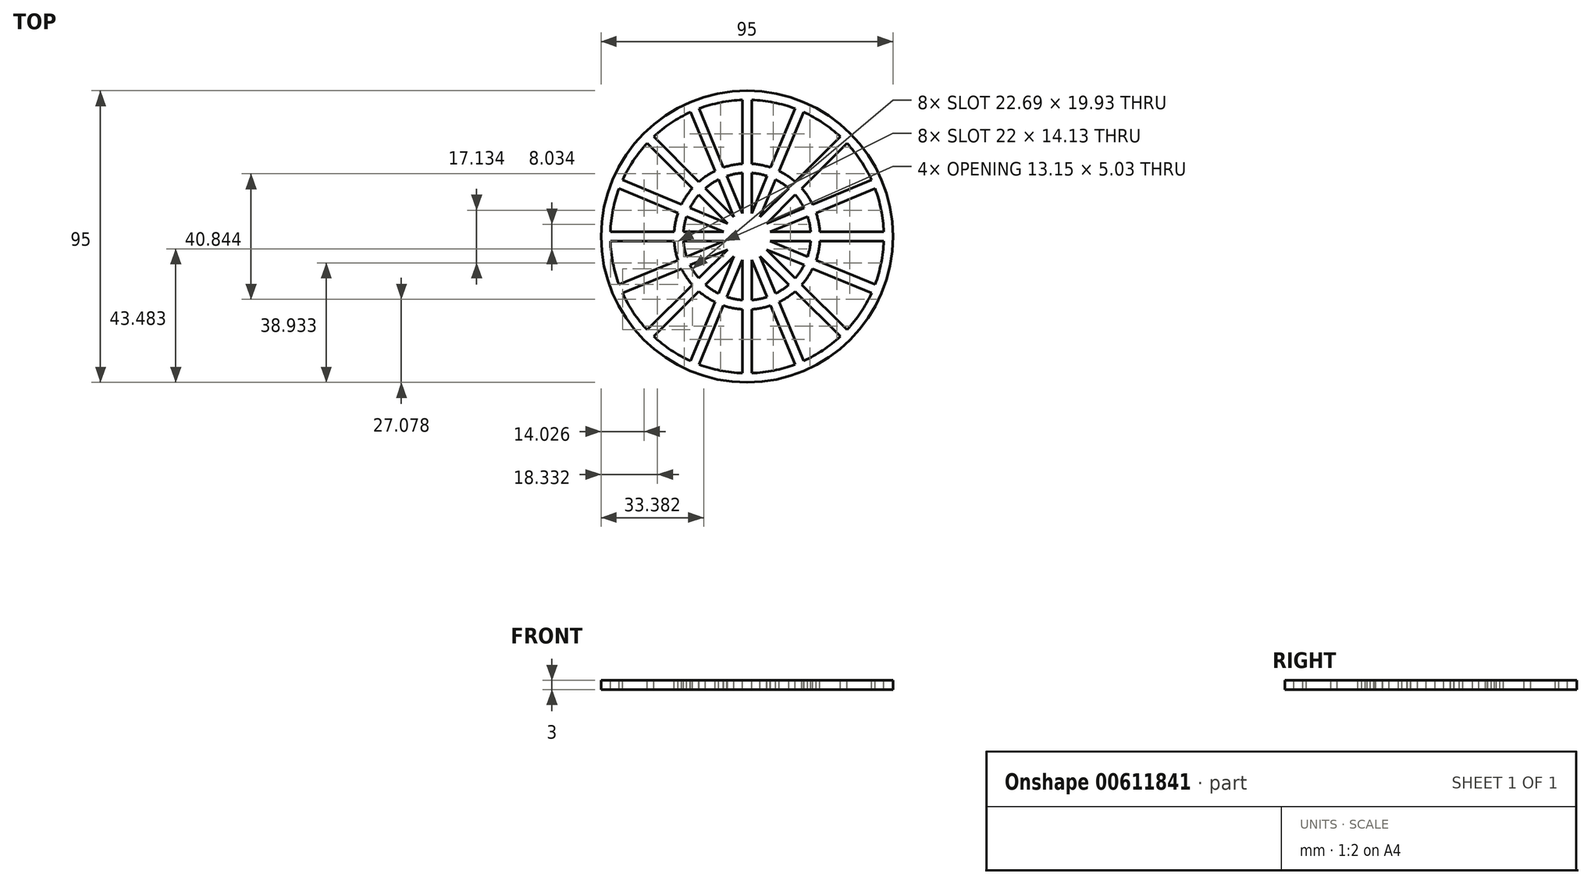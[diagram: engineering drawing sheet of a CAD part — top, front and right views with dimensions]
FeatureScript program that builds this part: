
annotation { "Feature Type Name" : "Feature", "Feature Type Description" : "" }
export const myFeature = defineFeature(function(context is Context, id is Id, definition is map)
    precondition{}
    {
        {
            assignVariable(context, id + "F0", {"name" : "b", "anyValue" : 3});
        }
        {
            var Q0;
            Q0=qCreatedBy(makeId("Top.planeOp"),FACE);
            var sketch = newSketch(context, id + "F1", { "sketchPlane" : qUnion([Q0])});
            skCircle(sketch, "E0", {"center": v(0, 0) * mm, "radius": 47.5 * mm});
            skCircle(sketch, "E1.0", {"center": v(0, 0) * mm, "radius": 44.5 * mm});
            skCircle(sketch, "E2", {"center": v(0, 0) * mm, "radius": 23.75 * mm});
            skCircle(sketch, "E3.0", {"center": v(0, 0) * mm, "radius": 20.75 * mm});
            skCircle(sketch, "E4", {"center": v(0, 0) * mm, "radius": 7.69 * mm});
            skLineSegment(sketch, "E5", {"start": v(0, 47.5) * mm, "end": v(0, -47.5) * mm, "construction": true});
            skLineSegment(sketch, "E6", {"start": v(1.5, 47.48) * mm, "end": v(1.5, 0) * mm});
            skLineSegment(sketch, "E7", {"start": v(1.5, 0) * mm, "end": v(-1.5, 0) * mm});
            skLineSegment(sketch, "E8", {"start": v(-1.5, 0) * mm, "end": v(-1.5, 47.48) * mm});
            skLineSegment(sketch, "E9.1.0", {"start": v(-1.39, -0.57) * mm, "end": v(-19.55, 43.29) * mm});
            skLineSegment(sketch, "E9.1.1", {"start": v(-16.78, 44.44) * mm, "end": v(1.39, 0.57) * mm});
            skLineSegment(sketch, "E9.2.0", {"start": v(-1.06, -1.06) * mm, "end": v(-34.63, 32.51) * mm});
            skLineSegment(sketch, "E9.2.1", {"start": v(-32.51, 34.63) * mm, "end": v(1.06, 1.06) * mm});
            skLineSegment(sketch, "E9.3.0", {"start": v(-0.57, -1.39) * mm, "end": v(-44.44, 16.78) * mm});
            skLineSegment(sketch, "E9.3.1", {"start": v(-43.29, 19.55) * mm, "end": v(0.57, 1.39) * mm});
            skLineSegment(sketch, "E9.4.0", {"start": v(0, -1.5) * mm, "end": v(-47.48, -1.5) * mm});
            skLineSegment(sketch, "E9.4.1", {"start": v(-47.48, 1.5) * mm, "end": v(0, 1.5) * mm});
            skLineSegment(sketch, "E9.5.0", {"start": v(0.57, -1.39) * mm, "end": v(-43.29, -19.55) * mm});
            skLineSegment(sketch, "E9.5.1", {"start": v(-44.44, -16.78) * mm, "end": v(-0.57, 1.39) * mm});
            skLineSegment(sketch, "E9.6.0", {"start": v(1.06, -1.06) * mm, "end": v(-32.51, -34.63) * mm});
            skLineSegment(sketch, "E9.6.1", {"start": v(-34.63, -32.51) * mm, "end": v(-1.06, 1.06) * mm});
            skLineSegment(sketch, "E9.7.0", {"start": v(1.39, -0.57) * mm, "end": v(-16.78, -44.44) * mm});
            skLineSegment(sketch, "E9.7.1", {"start": v(-19.55, -43.29) * mm, "end": v(-1.39, 0.57) * mm});
            skLineSegment(sketch, "E9.8.0", {"start": v(1.5, 0) * mm, "end": v(1.5, -47.48) * mm});
            skLineSegment(sketch, "E9.8.1", {"start": v(-1.5, -47.48) * mm, "end": v(-1.5, 0) * mm});
            skLineSegment(sketch, "E9.9.0", {"start": v(1.39, 0.57) * mm, "end": v(19.55, -43.29) * mm});
            skLineSegment(sketch, "E9.9.1", {"start": v(16.78, -44.44) * mm, "end": v(-1.39, -0.57) * mm});
            skLineSegment(sketch, "E9.10.0", {"start": v(1.06, 1.06) * mm, "end": v(34.63, -32.51) * mm});
            skLineSegment(sketch, "E9.10.1", {"start": v(32.51, -34.63) * mm, "end": v(-1.06, -1.06) * mm});
            skLineSegment(sketch, "E9.11.0", {"start": v(0.57, 1.39) * mm, "end": v(44.44, -16.78) * mm});
            skLineSegment(sketch, "E9.11.1", {"start": v(43.29, -19.55) * mm, "end": v(-0.57, -1.39) * mm});
            skLineSegment(sketch, "E9.12.0", {"start": v(0, 1.5) * mm, "end": v(47.48, 1.5) * mm});
            skLineSegment(sketch, "E9.12.1", {"start": v(47.48, -1.5) * mm, "end": v(0, -1.5) * mm});
            skLineSegment(sketch, "E9.13.0", {"start": v(-0.57, 1.39) * mm, "end": v(43.29, 19.55) * mm});
            skLineSegment(sketch, "E9.13.1", {"start": v(44.44, 16.78) * mm, "end": v(0.57, -1.39) * mm});
            skLineSegment(sketch, "E9.14.0", {"start": v(-1.06, 1.06) * mm, "end": v(32.51, 34.63) * mm});
            skLineSegment(sketch, "E9.14.1", {"start": v(34.63, 32.51) * mm, "end": v(1.06, -1.06) * mm});
            skLineSegment(sketch, "E9.15.0", {"start": v(-1.39, 0.57) * mm, "end": v(16.78, 44.44) * mm});
            skLineSegment(sketch, "E9.15.1", {"start": v(19.55, 43.29) * mm, "end": v(1.39, -0.57) * mm});
            skPoint(sketch, "E10", {"position": v(-1.5, 7.54) * mm});
            skSolve(sketch);
        }
        {
            var Q0;
            {var subQ0=sQuery(id+"F1.wireOp",EDGE,"E9.2.1");var subQ1=sQuery(id+"F1.wireOp",EDGE,"E1.0");var subQ2=makeQuery(id+"F1.imprint","INTERSECT",VERTEX,{"derivedFrom":[subQ1,subQ0]});Q0=makeQuery(id+"F1.imprint","IMPRINT",FACE,{"disambiguationData":[TD([[makeQuery(id+"F1.imprint","IMPRINT",EDGE,{"disambiguationData":[TD([[subQ2,-1.0]])],"derivedFrom":subQ1}),1.0]])]});}
            var Q1;
            {var subQ0=sQuery(id+"F1.wireOp",EDGE,"E9.2.1");var subQ1=sQuery(id+"F1.wireOp",EDGE,"E2");var subQ2=makeQuery(id+"F1.imprint","INTERSECT",VERTEX,{"derivedFrom":[subQ1,subQ0]});Q1=makeQuery(id+"F1.imprint","IMPRINT",FACE,{"disambiguationData":[TD([[makeQuery(id+"F1.imprint","IMPRINT",EDGE,{"disambiguationData":[TD([[subQ2,-1.0]])],"derivedFrom":subQ1}),1.0]])]});}
            var Q2;
            {var subQ0=sQuery(id+"F1.wireOp",EDGE,"E9.2.1");var subQ1=sQuery(id+"F1.wireOp",EDGE,"E3.0");var subQ2=makeQuery(id+"F1.imprint","INTERSECT",VERTEX,{"derivedFrom":[subQ1,subQ0]});Q2=makeQuery(id+"F1.imprint","IMPRINT",FACE,{"disambiguationData":[TD([[makeQuery(id+"F1.imprint","IMPRINT",EDGE,{"disambiguationData":[TD([[subQ2,-1.0]])],"derivedFrom":subQ1}),1.0]])]});}
            var Q3;
            {var subQ0=sQuery(id+"F1.wireOp",EDGE,"E8");var subQ3=sQuery(id+"F1.wireOp",EDGE,"E9.2.1");var subQ5=makeQuery(id+"F1.imprint","INTERSECT",VERTEX,{"derivedFrom":[subQ0,subQ3]});Q3=makeQuery(id+"F1.imprint","IMPRINT",FACE,{"disambiguationData":[TD([[makeQuery(id+"F1.imprint","IMPRINT",EDGE,{"disambiguationData":[TD([[subQ5,-1.0]])],"derivedFrom":subQ0}),1.0]])]});}
            var Q4;
            {var subQ0=sQuery(id+"F1.wireOp",EDGE,"E9.15.1");var subQ1=sQuery(id+"F1.wireOp",EDGE,"E9.12.0");var subQ2=makeQuery(id+"F1.imprint","INTERSECT",VERTEX,{"derivedFrom":[subQ1,subQ0]});Q4=makeQuery(id+"F1.imprint","IMPRINT",FACE,{"disambiguationData":[TD([[makeQuery(id+"F1.imprint","IMPRINT",EDGE,{"disambiguationData":[TD([[subQ2,-1.0]])],"derivedFrom":subQ1}),1.0]])]});}
            var Q5;
            {var subQ0=sQuery(id+"F1.wireOp",EDGE,"E9.9.1");var subQ1=sQuery(id+"F1.wireOp",EDGE,"E9.4.0");var subQ2=makeQuery(id+"F1.imprint","INTERSECT",VERTEX,{"derivedFrom":[subQ1,subQ0]});Q5=makeQuery(id+"F1.imprint","IMPRINT",FACE,{"disambiguationData":[TD([[makeQuery(id+"F1.imprint","IMPRINT",EDGE,{"disambiguationData":[TD([[subQ2,-1.0]])],"derivedFrom":subQ1}),1.0]])]});}
            var Q6;
            {var subQ0=sQuery(id+"F1.wireOp",EDGE,"E9.8.1");var subQ1=sQuery(id+"F1.wireOp",EDGE,"E9.2.0");var subQ2=makeQuery(id+"F1.imprint","INTERSECT",VERTEX,{"derivedFrom":[subQ1,subQ0]});Q6=makeQuery(id+"F1.imprint","IMPRINT",FACE,{"disambiguationData":[TD([[makeQuery(id+"F1.imprint","IMPRINT",EDGE,{"disambiguationData":[TD([[subQ2,-1.0]])],"derivedFrom":subQ1}),1.0]])]});}
            var Q7;
            {var subQ0=sQuery(id+"F1.wireOp",EDGE,"E9.5.0");var subQ3=sQuery(id+"F1.wireOp",EDGE,"E9.7.1");var subQ5=makeQuery(id+"F1.imprint","INTERSECT",VERTEX,{"derivedFrom":[subQ0,subQ3]});Q7=makeQuery(id+"F1.imprint","IMPRINT",FACE,{"disambiguationData":[TD([[makeQuery(id+"F1.imprint","IMPRINT",EDGE,{"disambiguationData":[TD([[subQ5,-1.0]])],"derivedFrom":subQ0}),1.0]])]});}
            var Q8;
            {var subQ0=sQuery(id+"F1.wireOp",EDGE,"E9.4.1");var subQ1=sQuery(id+"F1.wireOp",EDGE,"E9.1.0");var subQ2=makeQuery(id+"F1.imprint","INTERSECT",VERTEX,{"derivedFrom":[subQ1,subQ0]});Q8=makeQuery(id+"F1.imprint","IMPRINT",FACE,{"disambiguationData":[TD([[makeQuery(id+"F1.imprint","IMPRINT",EDGE,{"disambiguationData":[TD([[subQ2,-1.0]])],"derivedFrom":subQ1}),1.0]])]});}
            var Q9;
            {var subQ0=sQuery(id+"F1.wireOp",EDGE,"E9.7.1");var subQ1=sQuery(id+"F1.wireOp",EDGE,"E9.2.0");var subQ2=makeQuery(id+"F1.imprint","INTERSECT",VERTEX,{"derivedFrom":[subQ1,subQ0]});Q9=makeQuery(id+"F1.imprint","IMPRINT",FACE,{"disambiguationData":[TD([[makeQuery(id+"F1.imprint","IMPRINT",EDGE,{"disambiguationData":[TD([[subQ2,-1.0]])],"derivedFrom":subQ1}),1.0]])]});}
            var Q10;
            {var subQ0=sQuery(id+"F1.wireOp",EDGE,"E9.4.0");var subQ3=sQuery(id+"F1.wireOp",EDGE,"E9.6.1");var subQ5=makeQuery(id+"F1.imprint","INTERSECT",VERTEX,{"derivedFrom":[subQ0,subQ3]});Q10=makeQuery(id+"F1.imprint","IMPRINT",FACE,{"disambiguationData":[TD([[makeQuery(id+"F1.imprint","IMPRINT",EDGE,{"disambiguationData":[TD([[subQ5,-1.0]])],"derivedFrom":subQ0}),1.0]])]});}
            var Q11;
            {var subQ0=sQuery(id+"F1.wireOp",EDGE,"E9.13.0");var subQ1=sQuery(id+"F1.wireOp",EDGE,"E6");var subQ2=makeQuery(id+"F1.imprint","INTERSECT",VERTEX,{"derivedFrom":[subQ1,subQ0]});Q11=makeQuery(id+"F1.imprint","IMPRINT",FACE,{"disambiguationData":[TD([[makeQuery(id+"F1.imprint","IMPRINT",EDGE,{"disambiguationData":[TD([[subQ2,-1.0]])],"derivedFrom":subQ1}),-1.0]])]});}
            var Q12;
            {var subQ0=sQuery(id+"F1.wireOp",EDGE,"E9.7.1");var subQ1=sQuery(id+"F1.wireOp",EDGE,"E9.3.0");var subQ2=makeQuery(id+"F1.imprint","INTERSECT",VERTEX,{"derivedFrom":[subQ1,subQ0]});Q12=makeQuery(id+"F1.imprint","IMPRINT",FACE,{"disambiguationData":[TD([[makeQuery(id+"F1.imprint","IMPRINT",EDGE,{"disambiguationData":[TD([[subQ2,-1.0]])],"derivedFrom":subQ1}),1.0]])]});}
            var Q13;
            {var subQ0=sQuery(id+"F1.wireOp",EDGE,"E9.13.1");var subQ1=sQuery(id+"F1.wireOp",EDGE,"E9.9.0");var subQ2=makeQuery(id+"F1.imprint","INTERSECT",VERTEX,{"derivedFrom":[subQ1,subQ0]});Q13=makeQuery(id+"F1.imprint","IMPRINT",FACE,{"disambiguationData":[TD([[makeQuery(id+"F1.imprint","IMPRINT",EDGE,{"disambiguationData":[TD([[subQ2,-1.0]])],"derivedFrom":subQ1}),1.0]])]});}
            var Q14;
            {var subQ0=sQuery(id+"F1.wireOp",EDGE,"E9.3.0");var subQ3=sQuery(id+"F1.wireOp",EDGE,"E9.5.1");var subQ5=makeQuery(id+"F1.imprint","INTERSECT",VERTEX,{"derivedFrom":[subQ0,subQ3]});Q14=makeQuery(id+"F1.imprint","IMPRINT",FACE,{"disambiguationData":[TD([[makeQuery(id+"F1.imprint","IMPRINT",EDGE,{"disambiguationData":[TD([[subQ5,-1.0]])],"derivedFrom":subQ0}),1.0]])]});}
            var Q15;
            {var subQ0=sQuery(id+"F1.wireOp",EDGE,"E9.15.0");var subQ3=sQuery(id+"F1.wireOp",EDGE,"E9.1.1");var subQ5=makeQuery(id+"F1.imprint","INTERSECT",VERTEX,{"derivedFrom":[subQ3,subQ0]});Q15=makeQuery(id+"F1.imprint","IMPRINT",FACE,{"disambiguationData":[TD([[makeQuery(id+"F1.imprint","IMPRINT",EDGE,{"disambiguationData":[TD([[subQ5,1.0]])],"derivedFrom":subQ3}),1.0]])]});}
            var Q16;
            {var subQ0=sQuery(id+"F1.wireOp",EDGE,"E9.6.1");var subQ1=sQuery(id+"F1.wireOp",EDGE,"E9.3.0");var subQ2=makeQuery(id+"F1.imprint","INTERSECT",VERTEX,{"derivedFrom":[subQ1,subQ0]});Q16=makeQuery(id+"F1.imprint","IMPRINT",FACE,{"disambiguationData":[TD([[makeQuery(id+"F1.imprint","IMPRINT",EDGE,{"disambiguationData":[TD([[subQ2,-1.0]])],"derivedFrom":subQ1}),1.0]])]});}
            var Q17;
            {var subQ0=sQuery(id+"F1.wireOp",EDGE,"E9.11.1");var subQ1=sQuery(id+"F1.wireOp",EDGE,"E9.6.0");var subQ2=makeQuery(id+"F1.imprint","INTERSECT",VERTEX,{"derivedFrom":[subQ1,subQ0]});Q17=makeQuery(id+"F1.imprint","IMPRINT",FACE,{"disambiguationData":[TD([[makeQuery(id+"F1.imprint","IMPRINT",EDGE,{"disambiguationData":[TD([[subQ2,-1.0]])],"derivedFrom":subQ1}),1.0]])]});}
            var Q18;
            {var subQ0=sQuery(id+"F1.wireOp",EDGE,"E9.12.1");var subQ1=sQuery(id+"F1.wireOp",EDGE,"E9.9.0");var subQ2=makeQuery(id+"F1.imprint","INTERSECT",VERTEX,{"derivedFrom":[subQ1,subQ0]});Q18=makeQuery(id+"F1.imprint","IMPRINT",FACE,{"disambiguationData":[TD([[makeQuery(id+"F1.imprint","IMPRINT",EDGE,{"disambiguationData":[TD([[subQ2,-1.0]])],"derivedFrom":subQ1}),1.0]])]});}
            var Q19;
            {var subQ0=sQuery(id+"F1.wireOp",EDGE,"E9.8.1");var subQ1=sQuery(id+"F1.wireOp",EDGE,"E9.4.0");var subQ2=makeQuery(id+"F1.imprint","INTERSECT",VERTEX,{"derivedFrom":[subQ1,subQ0]});Q19=makeQuery(id+"F1.imprint","IMPRINT",FACE,{"disambiguationData":[TD([[makeQuery(id+"F1.imprint","IMPRINT",EDGE,{"disambiguationData":[TD([[subQ2,-1.0]])],"derivedFrom":subQ1}),1.0]])]});}
            var Q20;
            {var subQ0=sQuery(id+"F1.wireOp",EDGE,"E9.11.1");var subQ1=sQuery(id+"F1.wireOp",EDGE,"E9.7.0");var subQ2=makeQuery(id+"F1.imprint","INTERSECT",VERTEX,{"derivedFrom":[subQ1,subQ0]});Q20=makeQuery(id+"F1.imprint","IMPRINT",FACE,{"disambiguationData":[TD([[makeQuery(id+"F1.imprint","IMPRINT",EDGE,{"disambiguationData":[TD([[subQ2,-1.0]])],"derivedFrom":subQ1}),1.0]])]});}
            var Q21;
            {var subQ0=sQuery(id+"F1.wireOp",EDGE,"E9.15.0");var subQ1=sQuery(id+"F1.wireOp",EDGE,"E9.2.1");var subQ2=makeQuery(id+"F1.imprint","INTERSECT",VERTEX,{"derivedFrom":[subQ1,subQ0]});Q21=makeQuery(id+"F1.imprint","IMPRINT",FACE,{"disambiguationData":[TD([[makeQuery(id+"F1.imprint","IMPRINT",EDGE,{"disambiguationData":[TD([[subQ2,-1.0]])],"derivedFrom":subQ1}),-1.0]])]});}
            var Q22;
            {var subQ0=sQuery(id+"F1.wireOp",EDGE,"E9.3.1");var subQ1=sQuery(id+"F1.wireOp",EDGE,"E8");var subQ2=makeQuery(id+"F1.imprint","INTERSECT",VERTEX,{"derivedFrom":[subQ1,subQ0]});Q22=makeQuery(id+"F1.imprint","IMPRINT",FACE,{"disambiguationData":[TD([[makeQuery(id+"F1.imprint","IMPRINT",EDGE,{"disambiguationData":[TD([[subQ2,-1.0]])],"derivedFrom":subQ1}),-1.0]])]});}
            var Q23;
            {var subQ0=sQuery(id+"F1.wireOp",EDGE,"E9.13.0");var subQ1=sQuery(id+"F1.wireOp",EDGE,"E6");var subQ2=makeQuery(id+"F1.imprint","INTERSECT",VERTEX,{"derivedFrom":[subQ1,subQ0]});Q23=makeQuery(id+"F1.imprint","IMPRINT",FACE,{"disambiguationData":[TD([[makeQuery(id+"F1.imprint","IMPRINT",EDGE,{"disambiguationData":[TD([[subQ2,-1.0]])],"derivedFrom":subQ1}),1.0]])]});}
            var Q24;
            {var subQ0=sQuery(id+"F1.wireOp",EDGE,"E9.14.0");var subQ1=sQuery(id+"F1.wireOp",EDGE,"E6");var subQ2=makeQuery(id+"F1.imprint","INTERSECT",VERTEX,{"derivedFrom":[subQ1,subQ0]});Q24=makeQuery(id+"F1.imprint","IMPRINT",FACE,{"disambiguationData":[TD([[makeQuery(id+"F1.imprint","IMPRINT",EDGE,{"disambiguationData":[TD([[subQ2,-1.0]])],"derivedFrom":subQ1}),-1.0]])]});}
            var Q25;
            {var subQ0=sQuery(id+"F1.wireOp",EDGE,"E9.15.0");var subQ1=sQuery(id+"F1.wireOp",EDGE,"E9.1.1");var subQ2=makeQuery(id+"F1.imprint","INTERSECT",VERTEX,{"derivedFrom":[subQ1,subQ0]});Q25=makeQuery(id+"F1.imprint","IMPRINT",FACE,{"disambiguationData":[TD([[makeQuery(id+"F1.imprint","IMPRINT",EDGE,{"disambiguationData":[TD([[subQ2,-1.0]])],"derivedFrom":subQ1}),-1.0]])]});}
            var Q26;
            {var subQ0=sQuery(id+"F1.wireOp",EDGE,"E9.13.1");var subQ3=sQuery(id+"F1.wireOp",EDGE,"E9.11.0");var subQ5=makeQuery(id+"F1.imprint","INTERSECT",VERTEX,{"derivedFrom":[subQ3,subQ0]});Q26=makeQuery(id+"F1.imprint","IMPRINT",FACE,{"disambiguationData":[TD([[makeQuery(id+"F1.imprint","IMPRINT",EDGE,{"disambiguationData":[TD([[subQ5,-1.0]])],"derivedFrom":subQ3}),1.0]])]});}
            var Q27;
            {var subQ3=sQuery(id+"F1.wireOp",EDGE,"E9.15.0");var subQ5=sQuery(id+"F1.wireOp",EDGE,"E9.1.1");var subQ6=makeQuery(id+"F1.imprint","INTERSECT",VERTEX,{"derivedFrom":[subQ5,subQ3]});Q27=makeQuery(id+"F1.imprint","IMPRINT",FACE,{"disambiguationData":[TD([[makeQuery(id+"F1.imprint","IMPRINT",EDGE,{"disambiguationData":[TD([[subQ6,-1.0]])],"derivedFrom":subQ5}),1.0]])]});}
            var Q28;
            {var subQ0=sQuery(id+"F1.wireOp",EDGE,"E9.14.1");var subQ1=sQuery(id+"F1.wireOp",EDGE,"E9.11.0");var subQ2=makeQuery(id+"F1.imprint","INTERSECT",VERTEX,{"derivedFrom":[subQ1,subQ0]});Q28=makeQuery(id+"F1.imprint","IMPRINT",FACE,{"disambiguationData":[TD([[makeQuery(id+"F1.imprint","IMPRINT",EDGE,{"disambiguationData":[TD([[subQ2,-1.0]])],"derivedFrom":subQ1}),1.0]])]});}
            var Q29;
            {var subQ0=sQuery(id+"F1.wireOp",EDGE,"E9.11.1");var subQ1=sQuery(id+"F1.wireOp",EDGE,"E9.5.0");var subQ2=makeQuery(id+"F1.imprint","INTERSECT",VERTEX,{"derivedFrom":[subQ1,subQ0]});Q29=makeQuery(id+"F1.imprint","IMPRINT",FACE,{"disambiguationData":[TD([[makeQuery(id+"F1.imprint","IMPRINT",EDGE,{"disambiguationData":[TD([[subQ2,-1.0]])],"derivedFrom":subQ1}),1.0]])]});}
            var Q30;
            {var subQ0=sQuery(id+"F1.wireOp",EDGE,"E9.8.1");var subQ1=sQuery(id+"F1.wireOp",EDGE,"E9.3.0");var subQ2=makeQuery(id+"F1.imprint","INTERSECT",VERTEX,{"derivedFrom":[subQ1,subQ0]});Q30=makeQuery(id+"F1.imprint","IMPRINT",FACE,{"disambiguationData":[TD([[makeQuery(id+"F1.imprint","IMPRINT",EDGE,{"disambiguationData":[TD([[subQ2,-1.0]])],"derivedFrom":subQ1}),1.0]])]});}
            var Q31;
            {var subQ0=sQuery(id+"F1.wireOp",EDGE,"E9.14.1");var subQ1=sQuery(id+"F1.wireOp",EDGE,"E9.9.0");var subQ2=makeQuery(id+"F1.imprint","INTERSECT",VERTEX,{"derivedFrom":[subQ1,subQ0]});Q31=makeQuery(id+"F1.imprint","IMPRINT",FACE,{"disambiguationData":[TD([[makeQuery(id+"F1.imprint","IMPRINT",EDGE,{"disambiguationData":[TD([[subQ2,-1.0]])],"derivedFrom":subQ1}),1.0]])]});}
            var Q32;
            {var subQ0=sQuery(id+"F1.wireOp",EDGE,"E9.5.1");var subQ1=sQuery(id+"F1.wireOp",EDGE,"E9.2.0");var subQ2=makeQuery(id+"F1.imprint","INTERSECT",VERTEX,{"derivedFrom":[subQ1,subQ0]});Q32=makeQuery(id+"F1.imprint","IMPRINT",FACE,{"disambiguationData":[TD([[makeQuery(id+"F1.imprint","IMPRINT",EDGE,{"disambiguationData":[TD([[subQ2,-1.0]])],"derivedFrom":subQ1}),1.0]])]});}
            var Q33;
            {var subQ0=sQuery(id+"F1.wireOp",EDGE,"E9.3.1");var subQ1=sQuery(id+"F1.wireOp",EDGE,"E8");var subQ2=makeQuery(id+"F1.imprint","INTERSECT",VERTEX,{"derivedFrom":[subQ1,subQ0]});Q33=makeQuery(id+"F1.imprint","IMPRINT",FACE,{"disambiguationData":[TD([[makeQuery(id+"F1.imprint","IMPRINT",EDGE,{"disambiguationData":[TD([[subQ2,-1.0]])],"derivedFrom":subQ1}),1.0]])]});}
            var Q34;
            {var subQ0=sQuery(id+"F1.wireOp",EDGE,"E9.2.1");var subQ1=sQuery(id+"F1.wireOp",EDGE,"E8");var subQ2=makeQuery(id+"F1.imprint","INTERSECT",VERTEX,{"derivedFrom":[subQ1,subQ0]});Q34=makeQuery(id+"F1.imprint","IMPRINT",FACE,{"disambiguationData":[TD([[makeQuery(id+"F1.imprint","IMPRINT",EDGE,{"disambiguationData":[TD([[subQ2,-1.0]])],"derivedFrom":subQ0}),1.0]])]});}
            var Q35;
            {var subQ0=sQuery(id+"F1.wireOp",EDGE,"E9.12.0");var subQ1=sQuery(id+"F1.wireOp",EDGE,"E6");var subQ2=makeQuery(id+"F1.imprint","INTERSECT",VERTEX,{"derivedFrom":[subQ1,subQ0]});Q35=makeQuery(id+"F1.imprint","IMPRINT",FACE,{"disambiguationData":[TD([[makeQuery(id+"F1.imprint","IMPRINT",EDGE,{"disambiguationData":[TD([[subQ2,-1.0]])],"derivedFrom":subQ1}),-1.0]])]});}
            var Q36;
            {var subQ0=sQuery(id+"F1.wireOp",EDGE,"E9.13.1");var subQ1=sQuery(id+"F1.wireOp",EDGE,"E9.8.0");var subQ2=makeQuery(id+"F1.imprint","INTERSECT",VERTEX,{"derivedFrom":[subQ1,subQ0]});Q36=makeQuery(id+"F1.imprint","IMPRINT",FACE,{"disambiguationData":[TD([[makeQuery(id+"F1.imprint","IMPRINT",EDGE,{"disambiguationData":[TD([[subQ2,-1.0]])],"derivedFrom":subQ1}),1.0]])]});}
            var Q37;
            {var subQ0=sQuery(id+"F1.wireOp",EDGE,"E9.10.0");var subQ3=sQuery(id+"F1.wireOp",EDGE,"E9.12.1");var subQ5=makeQuery(id+"F1.imprint","INTERSECT",VERTEX,{"derivedFrom":[subQ0,subQ3]});Q37=makeQuery(id+"F1.imprint","IMPRINT",FACE,{"disambiguationData":[TD([[makeQuery(id+"F1.imprint","IMPRINT",EDGE,{"disambiguationData":[TD([[subQ5,-1.0]])],"derivedFrom":subQ0}),1.0]])]});}
            var Q38;
            {var subQ0=sQuery(id+"F1.wireOp",EDGE,"E9.14.0");var subQ3=sQuery(id+"F1.wireOp",EDGE,"E6");var subQ5=makeQuery(id+"F1.imprint","INTERSECT",VERTEX,{"derivedFrom":[subQ3,subQ0]});Q38=makeQuery(id+"F1.imprint","IMPRINT",FACE,{"disambiguationData":[TD([[makeQuery(id+"F1.imprint","IMPRINT",EDGE,{"disambiguationData":[TD([[subQ5,1.0]])],"derivedFrom":subQ3}),1.0]])]});}
            var Q39;
            {var subQ0=sQuery(id+"F1.wireOp",EDGE,"E9.12.1");var subQ1=sQuery(id+"F1.wireOp",EDGE,"E9.7.0");var subQ2=makeQuery(id+"F1.imprint","INTERSECT",VERTEX,{"derivedFrom":[subQ1,subQ0]});Q39=makeQuery(id+"F1.imprint","IMPRINT",FACE,{"disambiguationData":[TD([[makeQuery(id+"F1.imprint","IMPRINT",EDGE,{"disambiguationData":[TD([[subQ2,-1.0]])],"derivedFrom":subQ1}),1.0]])]});}
            var Q40;
            {var subQ0=sQuery(id+"F1.wireOp",EDGE,"E9.5.1");var subQ1=sQuery(id+"F1.wireOp",EDGE,"E9.1.0");var subQ2=makeQuery(id+"F1.imprint","INTERSECT",VERTEX,{"derivedFrom":[subQ1,subQ0]});Q40=makeQuery(id+"F1.imprint","IMPRINT",FACE,{"disambiguationData":[TD([[makeQuery(id+"F1.imprint","IMPRINT",EDGE,{"disambiguationData":[TD([[subQ2,-1.0]])],"derivedFrom":subQ1}),1.0]])]});}
            var Q41;
            {var subQ0=sQuery(id+"F1.wireOp",EDGE,"E9.5.1");var subQ1=sQuery(id+"F1.wireOp",EDGE,"E8");var subQ2=makeQuery(id+"F1.imprint","INTERSECT",VERTEX,{"derivedFrom":[subQ1,subQ0]});Q41=makeQuery(id+"F1.imprint","IMPRINT",FACE,{"disambiguationData":[TD([[makeQuery(id+"F1.imprint","IMPRINT",EDGE,{"disambiguationData":[TD([[subQ2,-1.0]])],"derivedFrom":subQ1}),1.0]])]});}
            var Q42;
            {var subQ0=sQuery(id+"F1.wireOp",EDGE,"E9.15.1");var subQ1=sQuery(id+"F1.wireOp",EDGE,"E9.11.0");var subQ2=makeQuery(id+"F1.imprint","INTERSECT",VERTEX,{"derivedFrom":[subQ1,subQ0]});Q42=makeQuery(id+"F1.imprint","IMPRINT",FACE,{"disambiguationData":[TD([[makeQuery(id+"F1.imprint","IMPRINT",EDGE,{"disambiguationData":[TD([[subQ2,-1.0]])],"derivedFrom":subQ1}),1.0]])]});}
            var Q43;
            {var subQ0=sQuery(id+"F1.wireOp",EDGE,"E9.13.0");var subQ3=sQuery(id+"F1.wireOp",EDGE,"E9.15.1");var subQ5=makeQuery(id+"F1.imprint","INTERSECT",VERTEX,{"derivedFrom":[subQ0,subQ3]});Q43=makeQuery(id+"F1.imprint","IMPRINT",FACE,{"disambiguationData":[TD([[makeQuery(id+"F1.imprint","IMPRINT",EDGE,{"disambiguationData":[TD([[subQ5,-1.0]])],"derivedFrom":subQ0}),1.0]])]});}
            var Q44;
            {var subQ0=sQuery(id+"F1.wireOp",EDGE,"E9.10.1");var subQ1=sQuery(id+"F1.wireOp",EDGE,"E9.7.0");var subQ2=makeQuery(id+"F1.imprint","INTERSECT",VERTEX,{"derivedFrom":[subQ1,subQ0]});Q44=makeQuery(id+"F1.imprint","IMPRINT",FACE,{"disambiguationData":[TD([[makeQuery(id+"F1.imprint","IMPRINT",EDGE,{"disambiguationData":[TD([[subQ2,-1.0]])],"derivedFrom":subQ1}),1.0]])]});}
            var Q45;
            {var subQ0=sQuery(id+"F1.wireOp",EDGE,"E9.14.0");var subQ1=sQuery(id+"F1.wireOp",EDGE,"E6");var subQ2=makeQuery(id+"F1.imprint","INTERSECT",VERTEX,{"derivedFrom":[subQ1,subQ0]});Q45=makeQuery(id+"F1.imprint","IMPRINT",FACE,{"disambiguationData":[TD([[makeQuery(id+"F1.imprint","IMPRINT",EDGE,{"disambiguationData":[TD([[subQ2,-1.0]])],"derivedFrom":subQ1}),1.0]])]});}
            var Q46;
            {var subQ0=sQuery(id+"F1.wireOp",EDGE,"E9.4.1");var subQ1=sQuery(id+"F1.wireOp",EDGE,"E8");var subQ2=makeQuery(id+"F1.imprint","INTERSECT",VERTEX,{"derivedFrom":[subQ1,subQ0]});Q46=makeQuery(id+"F1.imprint","IMPRINT",FACE,{"disambiguationData":[TD([[makeQuery(id+"F1.imprint","IMPRINT",EDGE,{"disambiguationData":[TD([[subQ2,-1.0]])],"derivedFrom":subQ1}),-1.0]])]});}
            var Q47;
            {var subQ0=sQuery(id+"F1.wireOp",EDGE,"E9.6.1");var subQ1=sQuery(id+"F1.wireOp",EDGE,"E9.2.0");var subQ2=makeQuery(id+"F1.imprint","INTERSECT",VERTEX,{"derivedFrom":[subQ1,subQ0]});Q47=makeQuery(id+"F1.imprint","IMPRINT",FACE,{"disambiguationData":[TD([[makeQuery(id+"F1.imprint","IMPRINT",EDGE,{"disambiguationData":[TD([[subQ2,-1.0]])],"derivedFrom":subQ1}),1.0]])]});}
            var Q48;
            {var subQ0=sQuery(id+"F1.wireOp",EDGE,"E9.7.1");var subQ1=sQuery(id+"F1.wireOp",EDGE,"E9.4.0");var subQ2=makeQuery(id+"F1.imprint","INTERSECT",VERTEX,{"derivedFrom":[subQ1,subQ0]});Q48=makeQuery(id+"F1.imprint","IMPRINT",FACE,{"disambiguationData":[TD([[makeQuery(id+"F1.imprint","IMPRINT",EDGE,{"disambiguationData":[TD([[subQ2,-1.0]])],"derivedFrom":subQ1}),1.0]])]});}
            var Q49;
            {var subQ0=sQuery(id+"F1.wireOp",EDGE,"E9.9.0");var subQ3=sQuery(id+"F1.wireOp",EDGE,"E9.11.1");var subQ5=makeQuery(id+"F1.imprint","INTERSECT",VERTEX,{"derivedFrom":[subQ0,subQ3]});Q49=makeQuery(id+"F1.imprint","IMPRINT",FACE,{"disambiguationData":[TD([[makeQuery(id+"F1.imprint","IMPRINT",EDGE,{"disambiguationData":[TD([[subQ5,-1.0]])],"derivedFrom":subQ0}),1.0]])]});}
            var Q50;
            {var subQ0=sQuery(id+"F1.wireOp",EDGE,"E9.14.1");var subQ3=sQuery(id+"F1.wireOp",EDGE,"E9.12.0");var subQ5=makeQuery(id+"F1.imprint","INTERSECT",VERTEX,{"derivedFrom":[subQ3,subQ0]});Q50=makeQuery(id+"F1.imprint","IMPRINT",FACE,{"disambiguationData":[TD([[makeQuery(id+"F1.imprint","IMPRINT",EDGE,{"disambiguationData":[TD([[subQ5,-1.0]])],"derivedFrom":subQ3}),1.0]])]});}
            var Q51;
            {var subQ0=sQuery(id+"F1.wireOp",EDGE,"E9.4.1");var subQ1=sQuery(id+"F1.wireOp",EDGE,"E8");var subQ2=makeQuery(id+"F1.imprint","INTERSECT",VERTEX,{"derivedFrom":[subQ1,subQ0]});Q51=makeQuery(id+"F1.imprint","IMPRINT",FACE,{"disambiguationData":[TD([[makeQuery(id+"F1.imprint","IMPRINT",EDGE,{"disambiguationData":[TD([[subQ2,-1.0]])],"derivedFrom":subQ1}),1.0]])]});}
            var Q52;
            {var subQ0=sQuery(id+"F1.wireOp",EDGE,"E9.2.0");var subQ3=sQuery(id+"F1.wireOp",EDGE,"E9.4.1");var subQ5=makeQuery(id+"F1.imprint","INTERSECT",VERTEX,{"derivedFrom":[subQ0,subQ3]});Q52=makeQuery(id+"F1.imprint","IMPRINT",FACE,{"disambiguationData":[TD([[makeQuery(id+"F1.imprint","IMPRINT",EDGE,{"disambiguationData":[TD([[subQ5,-1.0]])],"derivedFrom":subQ0}),1.0]])]});}
            var Q53;
            {var subQ0=sQuery(id+"F1.wireOp",EDGE,"E9.13.1");var subQ1=sQuery(id+"F1.wireOp",EDGE,"E9.10.0");var subQ2=makeQuery(id+"F1.imprint","INTERSECT",VERTEX,{"derivedFrom":[subQ1,subQ0]});Q53=makeQuery(id+"F1.imprint","IMPRINT",FACE,{"disambiguationData":[TD([[makeQuery(id+"F1.imprint","IMPRINT",EDGE,{"disambiguationData":[TD([[subQ2,-1.0]])],"derivedFrom":subQ1}),1.0]])]});}
            var Q54;
            {var subQ0=sQuery(id+"F1.wireOp",EDGE,"E9.8.1");var subQ1=sQuery(id+"F1.wireOp",EDGE,"E9.5.0");var subQ2=makeQuery(id+"F1.imprint","INTERSECT",VERTEX,{"derivedFrom":[subQ1,subQ0]});Q54=makeQuery(id+"F1.imprint","IMPRINT",FACE,{"disambiguationData":[TD([[makeQuery(id+"F1.imprint","IMPRINT",EDGE,{"disambiguationData":[TD([[subQ2,-1.0]])],"derivedFrom":subQ1}),1.0]])]});}
            var Q55;
            {var subQ0=sQuery(id+"F1.wireOp",EDGE,"E9.15.1");var subQ1=sQuery(id+"F1.wireOp",EDGE,"E9.9.0");var subQ2=makeQuery(id+"F1.imprint","INTERSECT",VERTEX,{"derivedFrom":[subQ1,subQ0]});Q55=makeQuery(id+"F1.imprint","IMPRINT",FACE,{"disambiguationData":[TD([[makeQuery(id+"F1.imprint","IMPRINT",EDGE,{"disambiguationData":[TD([[subQ2,-1.0]])],"derivedFrom":subQ1}),1.0]])]});}
            var Q56;
            {var subQ0=sQuery(id+"F1.wireOp",EDGE,"E9.8.0");var subQ3=sQuery(id+"F1.wireOp",EDGE,"E9.10.1");var subQ5=makeQuery(id+"F1.imprint","INTERSECT",VERTEX,{"derivedFrom":[subQ0,subQ3]});Q56=makeQuery(id+"F1.imprint","IMPRINT",FACE,{"disambiguationData":[TD([[makeQuery(id+"F1.imprint","IMPRINT",EDGE,{"disambiguationData":[TD([[subQ5,-1.0]])],"derivedFrom":subQ0}),1.0]])]});}
            var Q57;
            {var subQ0=sQuery(id+"F1.wireOp",EDGE,"E9.11.0");var subQ1=sQuery(id+"F1.wireOp",EDGE,"E6");var subQ2=makeQuery(id+"F1.imprint","INTERSECT",VERTEX,{"derivedFrom":[subQ1,subQ0]});Q57=makeQuery(id+"F1.imprint","IMPRINT",FACE,{"disambiguationData":[TD([[makeQuery(id+"F1.imprint","IMPRINT",EDGE,{"disambiguationData":[TD([[subQ2,-1.0]])],"derivedFrom":subQ1}),1.0]])]});}
            var Q58;
            {var subQ0=sQuery(id+"F1.wireOp",EDGE,"E9.6.1");var subQ1=sQuery(id+"F1.wireOp",EDGE,"E9.1.0");var subQ2=makeQuery(id+"F1.imprint","INTERSECT",VERTEX,{"derivedFrom":[subQ1,subQ0]});Q58=makeQuery(id+"F1.imprint","IMPRINT",FACE,{"disambiguationData":[TD([[makeQuery(id+"F1.imprint","IMPRINT",EDGE,{"disambiguationData":[TD([[subQ2,-1.0]])],"derivedFrom":subQ1}),1.0]])]});}
            var Q59;
            {var subQ0=sQuery(id+"F1.wireOp",EDGE,"E9.9.1");var subQ1=sQuery(id+"F1.wireOp",EDGE,"E9.6.0");var subQ2=makeQuery(id+"F1.imprint","INTERSECT",VERTEX,{"derivedFrom":[subQ1,subQ0]});Q59=makeQuery(id+"F1.imprint","IMPRINT",FACE,{"disambiguationData":[TD([[makeQuery(id+"F1.imprint","IMPRINT",EDGE,{"disambiguationData":[TD([[subQ2,-1.0]])],"derivedFrom":subQ1}),1.0]])]});}
            var Q60;
            {var subQ0=sQuery(id+"F1.wireOp",EDGE,"E9.14.1");var subQ1=sQuery(id+"F1.wireOp",EDGE,"E9.10.0");var subQ2=makeQuery(id+"F1.imprint","INTERSECT",VERTEX,{"derivedFrom":[subQ1,subQ0]});Q60=makeQuery(id+"F1.imprint","IMPRINT",FACE,{"disambiguationData":[TD([[makeQuery(id+"F1.imprint","IMPRINT",EDGE,{"disambiguationData":[TD([[subQ2,-1.0]])],"derivedFrom":subQ1}),1.0]])]});}
            var Q61;
            {var subQ0=sQuery(id+"F1.wireOp",EDGE,"E9.6.1");var subQ1=sQuery(id+"F1.wireOp",EDGE,"E8");var subQ2=makeQuery(id+"F1.imprint","INTERSECT",VERTEX,{"derivedFrom":[subQ1,subQ0]});Q61=makeQuery(id+"F1.imprint","IMPRINT",FACE,{"disambiguationData":[TD([[makeQuery(id+"F1.imprint","IMPRINT",EDGE,{"disambiguationData":[TD([[subQ2,-1.0]])],"derivedFrom":subQ1}),1.0]])]});}
            var Q62;
            {var subQ0=sQuery(id+"F1.wireOp",EDGE,"E9.7.0");var subQ3=sQuery(id+"F1.wireOp",EDGE,"E9.9.1");var subQ5=makeQuery(id+"F1.imprint","INTERSECT",VERTEX,{"derivedFrom":[subQ0,subQ3]});Q62=makeQuery(id+"F1.imprint","IMPRINT",FACE,{"disambiguationData":[TD([[makeQuery(id+"F1.imprint","IMPRINT",EDGE,{"disambiguationData":[TD([[subQ5,-1.0]])],"derivedFrom":subQ0}),1.0]])]});}
            var Q63;
            {var subQ0=sQuery(id+"F1.wireOp",EDGE,"E9.11.1");var subQ1=sQuery(id+"F1.wireOp",EDGE,"E9.8.0");var subQ2=makeQuery(id+"F1.imprint","INTERSECT",VERTEX,{"derivedFrom":[subQ1,subQ0]});Q63=makeQuery(id+"F1.imprint","IMPRINT",FACE,{"disambiguationData":[TD([[makeQuery(id+"F1.imprint","IMPRINT",EDGE,{"disambiguationData":[TD([[subQ2,-1.0]])],"derivedFrom":subQ1}),1.0]])]});}
            var Q64;
            {var subQ0=sQuery(id+"F1.wireOp",EDGE,"E9.9.1");var subQ1=sQuery(id+"F1.wireOp",EDGE,"E9.5.0");var subQ2=makeQuery(id+"F1.imprint","INTERSECT",VERTEX,{"derivedFrom":[subQ1,subQ0]});Q64=makeQuery(id+"F1.imprint","IMPRINT",FACE,{"disambiguationData":[TD([[makeQuery(id+"F1.imprint","IMPRINT",EDGE,{"disambiguationData":[TD([[subQ2,-1.0]])],"derivedFrom":subQ1}),1.0]])]});}
            var Q65;
            {var subQ0=sQuery(id+"F1.wireOp",EDGE,"E9.1.0");var subQ3=sQuery(id+"F1.wireOp",EDGE,"E9.3.1");var subQ5=makeQuery(id+"F1.imprint","INTERSECT",VERTEX,{"derivedFrom":[subQ0,subQ3]});Q65=makeQuery(id+"F1.imprint","IMPRINT",FACE,{"disambiguationData":[TD([[makeQuery(id+"F1.imprint","IMPRINT",EDGE,{"disambiguationData":[TD([[subQ5,-1.0]])],"derivedFrom":subQ0}),1.0]])]});}
            var Q66;
            {var subQ0=sQuery(id+"F1.wireOp",EDGE,"E9.15.0");var subQ1=sQuery(id+"F1.wireOp",EDGE,"E9.3.1");var subQ2=makeQuery(id+"F1.imprint","INTERSECT",VERTEX,{"derivedFrom":[subQ1,subQ0]});Q66=makeQuery(id+"F1.imprint","IMPRINT",FACE,{"disambiguationData":[TD([[makeQuery(id+"F1.imprint","IMPRINT",EDGE,{"disambiguationData":[TD([[subQ2,-1.0]])],"derivedFrom":subQ1}),-1.0]])]});}
            var Q67;
            {var subQ0=sQuery(id+"F1.wireOp",EDGE,"E9.10.1");var subQ1=sQuery(id+"F1.wireOp",EDGE,"E9.6.0");var subQ2=makeQuery(id+"F1.imprint","INTERSECT",VERTEX,{"derivedFrom":[subQ1,subQ0]});Q67=makeQuery(id+"F1.imprint","IMPRINT",FACE,{"disambiguationData":[TD([[makeQuery(id+"F1.imprint","IMPRINT",EDGE,{"disambiguationData":[TD([[subQ2,-1.0]])],"derivedFrom":subQ1}),1.0]])]});}
            var Q68;
            {var subQ0=sQuery(id+"F1.wireOp",EDGE,"E9.15.1");var subQ1=sQuery(id+"F1.wireOp",EDGE,"E9.10.0");var subQ2=makeQuery(id+"F1.imprint","INTERSECT",VERTEX,{"derivedFrom":[subQ1,subQ0]});Q68=makeQuery(id+"F1.imprint","IMPRINT",FACE,{"disambiguationData":[TD([[makeQuery(id+"F1.imprint","IMPRINT",EDGE,{"disambiguationData":[TD([[subQ2,-1.0]])],"derivedFrom":subQ1}),1.0]])]});}
            var Q69;
            {var subQ0=sQuery(id+"F1.wireOp",EDGE,"E9.14.0");var subQ1=sQuery(id+"F1.wireOp",EDGE,"E9.1.1");var subQ2=makeQuery(id+"F1.imprint","INTERSECT",VERTEX,{"derivedFrom":[subQ1,subQ0]});Q69=makeQuery(id+"F1.imprint","IMPRINT",FACE,{"disambiguationData":[TD([[makeQuery(id+"F1.imprint","IMPRINT",EDGE,{"disambiguationData":[TD([[subQ2,-1.0]])],"derivedFrom":subQ1}),-1.0]])]});}
            var Q70;
            {var subQ0=sQuery(id+"F1.wireOp",EDGE,"E9.12.1");var subQ1=sQuery(id+"F1.wireOp",EDGE,"E9.8.0");var subQ2=makeQuery(id+"F1.imprint","INTERSECT",VERTEX,{"derivedFrom":[subQ1,subQ0]});Q70=makeQuery(id+"F1.imprint","IMPRINT",FACE,{"disambiguationData":[TD([[makeQuery(id+"F1.imprint","IMPRINT",EDGE,{"disambiguationData":[TD([[subQ2,-1.0]])],"derivedFrom":subQ1}),1.0]])]});}
            var Q71;
            {var subQ0=sQuery(id+"F1.wireOp",EDGE,"E9.12.0");var subQ1=sQuery(id+"F1.wireOp",EDGE,"E6");var subQ2=makeQuery(id+"F1.imprint","INTERSECT",VERTEX,{"derivedFrom":[subQ1,subQ0]});Q71=makeQuery(id+"F1.imprint","IMPRINT",FACE,{"disambiguationData":[TD([[makeQuery(id+"F1.imprint","IMPRINT",EDGE,{"disambiguationData":[TD([[subQ2,-1.0]])],"derivedFrom":subQ1}),1.0]])]});}
            var Q72;
            {var subQ0=sQuery(id+"F1.wireOp",EDGE,"E9.6.0");var subQ3=sQuery(id+"F1.wireOp",EDGE,"E9.8.1");var subQ5=makeQuery(id+"F1.imprint","INTERSECT",VERTEX,{"derivedFrom":[subQ0,subQ3]});Q72=makeQuery(id+"F1.imprint","IMPRINT",FACE,{"disambiguationData":[TD([[makeQuery(id+"F1.imprint","IMPRINT",EDGE,{"disambiguationData":[TD([[subQ5,-1.0]])],"derivedFrom":subQ0}),1.0]])]});}
            var Q73;
            {var subQ0=sQuery(id+"F1.wireOp",EDGE,"E9.10.1");var subQ1=sQuery(id+"F1.wireOp",EDGE,"E9.5.0");var subQ2=makeQuery(id+"F1.imprint","INTERSECT",VERTEX,{"derivedFrom":[subQ1,subQ0]});Q73=makeQuery(id+"F1.imprint","IMPRINT",FACE,{"disambiguationData":[TD([[makeQuery(id+"F1.imprint","IMPRINT",EDGE,{"disambiguationData":[TD([[subQ2,-1.0]])],"derivedFrom":subQ1}),1.0]])]});}
            var Q74;
            {var subQ0=sQuery(id+"F1.wireOp",EDGE,"E9.5.1");var subQ1=sQuery(id+"F1.wireOp",EDGE,"E8");var subQ2=makeQuery(id+"F1.imprint","INTERSECT",VERTEX,{"derivedFrom":[subQ1,subQ0]});Q74=makeQuery(id+"F1.imprint","IMPRINT",FACE,{"disambiguationData":[TD([[makeQuery(id+"F1.imprint","IMPRINT",EDGE,{"disambiguationData":[TD([[subQ2,-1.0]])],"derivedFrom":subQ1}),-1.0]])]});}
            var Q75;
            {var subQ0=sQuery(id+"F1.wireOp",EDGE,"E9.14.1");var subQ1=sQuery(id+"F1.wireOp",EDGE,"E9.8.0");var subQ2=makeQuery(id+"F1.imprint","INTERSECT",VERTEX,{"derivedFrom":[subQ1,subQ0]});Q75=makeQuery(id+"F1.imprint","IMPRINT",FACE,{"disambiguationData":[TD([[makeQuery(id+"F1.imprint","IMPRINT",EDGE,{"disambiguationData":[TD([[subQ2,-1.0]])],"derivedFrom":subQ1}),1.0]])]});}
            var Q76;
            {var subQ0=sQuery(id+"F1.wireOp",EDGE,"E9.10.1");var subQ1=sQuery(id+"F1.wireOp",EDGE,"E9.4.0");var subQ2=makeQuery(id+"F1.imprint","INTERSECT",VERTEX,{"derivedFrom":[subQ1,subQ0]});Q76=makeQuery(id+"F1.imprint","IMPRINT",FACE,{"disambiguationData":[TD([[makeQuery(id+"F1.imprint","IMPRINT",EDGE,{"disambiguationData":[TD([[subQ2,-1.0]])],"derivedFrom":subQ1}),1.0]])]});}
            var Q77;
            {var subQ1=sQuery(id+"F1.wireOp",EDGE,"E7");Q77=makeQuery(id+"F1.imprint","IMPRINT",FACE,{"disambiguationData":[TD([[makeQuery(id+"F1.imprint","IMPRINT",EDGE,{"derivedFrom":subQ1}),1.0]])]});}
            var Q78;
            {var subQ0=sQuery(id+"F1.wireOp",EDGE,"E9.14.0");var subQ1=sQuery(id+"F1.wireOp",EDGE,"E9.2.1");var subQ2=makeQuery(id+"F1.imprint","INTERSECT",VERTEX,{"derivedFrom":[subQ1,subQ0]});Q78=makeQuery(id+"F1.imprint","IMPRINT",FACE,{"disambiguationData":[TD([[makeQuery(id+"F1.imprint","IMPRINT",EDGE,{"disambiguationData":[TD([[subQ2,-1.0]])],"derivedFrom":subQ1}),-1.0]])]});}
            var Q79;
            {var subQ0=sQuery(id+"F1.wireOp",EDGE,"E9.13.1");var subQ1=sQuery(id+"F1.wireOp",EDGE,"E9.7.0");var subQ2=makeQuery(id+"F1.imprint","INTERSECT",VERTEX,{"derivedFrom":[subQ1,subQ0]});Q79=makeQuery(id+"F1.imprint","IMPRINT",FACE,{"disambiguationData":[TD([[makeQuery(id+"F1.imprint","IMPRINT",EDGE,{"disambiguationData":[TD([[subQ2,-1.0]])],"derivedFrom":subQ1}),1.0]])]});}
            var Q80;
            {var subQ0=sQuery(id+"F1.wireOp",EDGE,"E7");Q80=makeQuery(id+"F1.imprint","IMPRINT",FACE,{"disambiguationData":[TD([[makeQuery(id+"F1.imprint","IMPRINT",EDGE,{"derivedFrom":subQ0}),-1.0]])]});}
            var Q81;
            {var subQ0=sQuery(id+"F1.wireOp",EDGE,"E9.9.1");var subQ1=sQuery(id+"F1.wireOp",EDGE,"E9.3.0");var subQ2=makeQuery(id+"F1.imprint","INTERSECT",VERTEX,{"derivedFrom":[subQ1,subQ0]});Q81=makeQuery(id+"F1.imprint","IMPRINT",FACE,{"disambiguationData":[TD([[makeQuery(id+"F1.imprint","IMPRINT",EDGE,{"disambiguationData":[TD([[subQ2,-1.0]])],"derivedFrom":subQ1}),1.0]])]});}
            var Q82;
            {var subQ0=sQuery(id+"F1.wireOp",EDGE,"E9.13.0");var subQ1=sQuery(id+"F1.wireOp",EDGE,"E9.1.1");var subQ2=makeQuery(id+"F1.imprint","INTERSECT",VERTEX,{"derivedFrom":[subQ1,subQ0]});Q82=makeQuery(id+"F1.imprint","IMPRINT",FACE,{"disambiguationData":[TD([[makeQuery(id+"F1.imprint","IMPRINT",EDGE,{"disambiguationData":[TD([[subQ2,-1.0]])],"derivedFrom":subQ1}),-1.0]])]});}
            var Q83;
            {var subQ0=sQuery(id+"F1.wireOp",EDGE,"E9.7.1");var subQ1=sQuery(id+"F1.wireOp",EDGE,"E9.1.0");var subQ2=makeQuery(id+"F1.imprint","INTERSECT",VERTEX,{"derivedFrom":[subQ1,subQ0]});Q83=makeQuery(id+"F1.imprint","IMPRINT",FACE,{"disambiguationData":[TD([[makeQuery(id+"F1.imprint","IMPRINT",EDGE,{"disambiguationData":[TD([[subQ2,-1.0]])],"derivedFrom":subQ1}),1.0]])]});}
            var Q84;
            {var subQ0=sQuery(id+"F1.wireOp",EDGE,"E9.10.1");var subQ1=sQuery(id+"F1.wireOp",EDGE,"E9.2.0");var subQ2=makeQuery(id+"F1.imprint","INTERSECT",VERTEX,{"derivedFrom":[subQ1,subQ0]});Q84=makeQuery(id+"F1.imprint","IMPRINT",FACE,{"disambiguationData":[TD([[makeQuery(id+"F1.imprint","IMPRINT",EDGE,{"disambiguationData":[TD([[subQ2,-1.0]])],"derivedFrom":subQ1}),1.0]])]});}
            var Q85;
            {var subQ0=sQuery(id+"F1.wireOp",EDGE,"E9.12.1");var subQ1=sQuery(id+"F1.wireOp",EDGE,"E9.4.0");var subQ2=makeQuery(id+"F1.imprint","INTERSECT",VERTEX,{"derivedFrom":[subQ1,subQ0]});Q85=makeQuery(id+"F1.imprint","IMPRINT",FACE,{"disambiguationData":[TD([[makeQuery(id+"F1.imprint","IMPRINT",EDGE,{"disambiguationData":[TD([[subQ2,-1.0]])],"derivedFrom":subQ1}),1.0]])]});}
            var Q86;
            {var subQ0=sQuery(id+"F1.wireOp",EDGE,"E9.12.1");var subQ1=sQuery(id+"F1.wireOp",EDGE,"E9.6.0");var subQ2=makeQuery(id+"F1.imprint","INTERSECT",VERTEX,{"derivedFrom":[subQ1,subQ0]});Q86=makeQuery(id+"F1.imprint","IMPRINT",FACE,{"disambiguationData":[TD([[makeQuery(id+"F1.imprint","IMPRINT",EDGE,{"disambiguationData":[TD([[subQ2,-1.0]])],"derivedFrom":subQ1}),1.0]])]});}
            var Q87;
            {var subQ0=sQuery(id+"F1.wireOp",EDGE,"E9.13.0");var subQ1=sQuery(id+"F1.wireOp",EDGE,"E9.3.1");var subQ2=makeQuery(id+"F1.imprint","INTERSECT",VERTEX,{"derivedFrom":[subQ1,subQ0]});Q87=makeQuery(id+"F1.imprint","IMPRINT",FACE,{"disambiguationData":[TD([[makeQuery(id+"F1.imprint","IMPRINT",EDGE,{"disambiguationData":[TD([[subQ2,-1.0]])],"derivedFrom":subQ1}),-1.0]])]});}
            var Q88;
            {var subQ0=sQuery(id+"F1.wireOp",EDGE,"E9.11.0");var subQ1=sQuery(id+"F1.wireOp",EDGE,"E9.1.1");var subQ2=makeQuery(id+"F1.imprint","INTERSECT",VERTEX,{"derivedFrom":[subQ1,subQ0]});Q88=makeQuery(id+"F1.imprint","IMPRINT",FACE,{"disambiguationData":[TD([[makeQuery(id+"F1.imprint","IMPRINT",EDGE,{"disambiguationData":[TD([[subQ2,-1.0]])],"derivedFrom":subQ1}),-1.0]])]});}
            var Q89;
            {var subQ0=sQuery(id+"F1.wireOp",EDGE,"E9.12.1");var subQ1=sQuery(id+"F1.wireOp",EDGE,"E9.5.0");var subQ2=makeQuery(id+"F1.imprint","INTERSECT",VERTEX,{"derivedFrom":[subQ1,subQ0]});Q89=makeQuery(id+"F1.imprint","IMPRINT",FACE,{"disambiguationData":[TD([[makeQuery(id+"F1.imprint","IMPRINT",EDGE,{"disambiguationData":[TD([[subQ2,-1.0]])],"derivedFrom":subQ1}),1.0]])]});}
            var Q90;
            {var subQ0=sQuery(id+"F1.wireOp",EDGE,"E9.14.0");var subQ1=sQuery(id+"F1.wireOp",EDGE,"E9.4.1");var subQ2=makeQuery(id+"F1.imprint","INTERSECT",VERTEX,{"derivedFrom":[subQ1,subQ0]});Q90=makeQuery(id+"F1.imprint","IMPRINT",FACE,{"disambiguationData":[TD([[makeQuery(id+"F1.imprint","IMPRINT",EDGE,{"disambiguationData":[TD([[subQ2,-1.0]])],"derivedFrom":subQ1}),-1.0]])]});}
            var Q91;
            {var subQ0=sQuery(id+"F1.wireOp",EDGE,"E9.13.1");var subQ1=sQuery(id+"F1.wireOp",EDGE,"E9.6.0");var subQ2=makeQuery(id+"F1.imprint","INTERSECT",VERTEX,{"derivedFrom":[subQ1,subQ0]});Q91=makeQuery(id+"F1.imprint","IMPRINT",FACE,{"disambiguationData":[TD([[makeQuery(id+"F1.imprint","IMPRINT",EDGE,{"disambiguationData":[TD([[subQ2,-1.0]])],"derivedFrom":subQ1}),1.0]])]});}
            var Q92;
            {var subQ0=sQuery(id+"F1.wireOp",EDGE,"E9.15.0");var subQ1=sQuery(id+"F1.wireOp",EDGE,"E9.4.1");var subQ2=makeQuery(id+"F1.imprint","INTERSECT",VERTEX,{"derivedFrom":[subQ1,subQ0]});Q92=makeQuery(id+"F1.imprint","IMPRINT",FACE,{"disambiguationData":[TD([[makeQuery(id+"F1.imprint","IMPRINT",EDGE,{"disambiguationData":[TD([[subQ2,-1.0]])],"derivedFrom":subQ1}),-1.0]])]});}
            var Q93;
            {var subQ0=sQuery(id+"F1.wireOp",EDGE,"E9.9.1");var subQ1=sQuery(id+"F1.wireOp",EDGE,"E9.2.0");var subQ2=makeQuery(id+"F1.imprint","INTERSECT",VERTEX,{"derivedFrom":[subQ1,subQ0]});Q93=makeQuery(id+"F1.imprint","IMPRINT",FACE,{"disambiguationData":[TD([[makeQuery(id+"F1.imprint","IMPRINT",EDGE,{"disambiguationData":[TD([[subQ2,-1.0]])],"derivedFrom":subQ1}),1.0]])]});}
            var Q94;
            {var subQ0=sQuery(id+"F1.wireOp",EDGE,"E9.7.1");var subQ1=sQuery(id+"F1.wireOp",EDGE,"E8");var subQ2=makeQuery(id+"F1.imprint","INTERSECT",VERTEX,{"derivedFrom":[subQ1,subQ0]});Q94=makeQuery(id+"F1.imprint","IMPRINT",FACE,{"disambiguationData":[TD([[makeQuery(id+"F1.imprint","IMPRINT",EDGE,{"disambiguationData":[TD([[subQ2,-1.0]])],"derivedFrom":subQ1}),-1.0]])]});}
            var Q95;
            {var subQ0=sQuery(id+"F1.wireOp",EDGE,"E9.10.0");var subQ1=sQuery(id+"F1.wireOp",EDGE,"E6");var subQ2=makeQuery(id+"F1.imprint","INTERSECT",VERTEX,{"derivedFrom":[subQ1,subQ0]});Q95=makeQuery(id+"F1.imprint","IMPRINT",FACE,{"disambiguationData":[TD([[makeQuery(id+"F1.imprint","IMPRINT",EDGE,{"disambiguationData":[TD([[subQ2,-1.0]])],"derivedFrom":subQ1}),-1.0]])]});}
            var Q96;
            {var subQ0=sQuery(id+"F1.wireOp",EDGE,"E9.15.1");var subQ1=sQuery(id+"F1.wireOp",EDGE,"E9.7.0");var subQ2=makeQuery(id+"F1.imprint","INTERSECT",VERTEX,{"derivedFrom":[subQ1,subQ0]});Q96=makeQuery(id+"F1.imprint","IMPRINT",FACE,{"disambiguationData":[TD([[makeQuery(id+"F1.imprint","IMPRINT",EDGE,{"disambiguationData":[TD([[subQ2,-1.0]])],"derivedFrom":subQ1}),1.0]])]});}
            var Q97;
            {var subQ0=sQuery(id+"F1.wireOp",EDGE,"E9.11.1");var subQ1=sQuery(id+"F1.wireOp",EDGE,"E9.4.0");var subQ2=makeQuery(id+"F1.imprint","INTERSECT",VERTEX,{"derivedFrom":[subQ1,subQ0]});Q97=makeQuery(id+"F1.imprint","IMPRINT",FACE,{"disambiguationData":[TD([[makeQuery(id+"F1.imprint","IMPRINT",EDGE,{"disambiguationData":[TD([[subQ2,-1.0]])],"derivedFrom":subQ1}),1.0]])]});}
            var Q98;
            {var subQ0=sQuery(id+"F1.wireOp",EDGE,"E9.14.1");var subQ1=sQuery(id+"F1.wireOp",EDGE,"E9.7.0");var subQ2=makeQuery(id+"F1.imprint","INTERSECT",VERTEX,{"derivedFrom":[subQ1,subQ0]});Q98=makeQuery(id+"F1.imprint","IMPRINT",FACE,{"disambiguationData":[TD([[makeQuery(id+"F1.imprint","IMPRINT",EDGE,{"disambiguationData":[TD([[subQ2,-1.0]])],"derivedFrom":subQ1}),1.0]])]});}
            var Q99;
            {var subQ0=sQuery(id+"F1.wireOp",EDGE,"E9.6.1");var subQ1=sQuery(id+"F1.wireOp",EDGE,"E8");var subQ2=makeQuery(id+"F1.imprint","INTERSECT",VERTEX,{"derivedFrom":[subQ1,subQ0]});Q99=makeQuery(id+"F1.imprint","IMPRINT",FACE,{"disambiguationData":[TD([[makeQuery(id+"F1.imprint","IMPRINT",EDGE,{"disambiguationData":[TD([[subQ2,-1.0]])],"derivedFrom":subQ1}),-1.0]])]});}
            var Q100;
            {var subQ0=sQuery(id+"F1.wireOp",EDGE,"E9.12.0");var subQ1=sQuery(id+"F1.wireOp",EDGE,"E9.1.1");var subQ2=makeQuery(id+"F1.imprint","INTERSECT",VERTEX,{"derivedFrom":[subQ1,subQ0]});Q100=makeQuery(id+"F1.imprint","IMPRINT",FACE,{"disambiguationData":[TD([[makeQuery(id+"F1.imprint","IMPRINT",EDGE,{"disambiguationData":[TD([[subQ2,-1.0]])],"derivedFrom":subQ1}),-1.0]])]});}
            var Q101;
            {var subQ0=sQuery(id+"F1.wireOp",EDGE,"E9.14.1");var subQ1=sQuery(id+"F1.wireOp",EDGE,"E9.6.0");var subQ2=makeQuery(id+"F1.imprint","INTERSECT",VERTEX,{"derivedFrom":[subQ1,subQ0]});Q101=makeQuery(id+"F1.imprint","IMPRINT",FACE,{"disambiguationData":[TD([[makeQuery(id+"F1.imprint","IMPRINT",EDGE,{"disambiguationData":[TD([[subQ2,-1.0]])],"derivedFrom":subQ1}),1.0]])]});}
            var Q102;
            {var subQ0=sQuery(id+"F1.wireOp",EDGE,"E9.11.1");var subQ1=sQuery(id+"F1.wireOp",EDGE,"E9.3.0");var subQ2=makeQuery(id+"F1.imprint","INTERSECT",VERTEX,{"derivedFrom":[subQ1,subQ0]});Q102=makeQuery(id+"F1.imprint","IMPRINT",FACE,{"disambiguationData":[TD([[makeQuery(id+"F1.imprint","IMPRINT",EDGE,{"disambiguationData":[TD([[subQ2,-1.0]])],"derivedFrom":subQ1}),1.0]])]});}
            var Q103;
            {var subQ0=sQuery(id+"F1.wireOp",EDGE,"E9.14.0");var subQ1=sQuery(id+"F1.wireOp",EDGE,"E9.3.1");var subQ2=makeQuery(id+"F1.imprint","INTERSECT",VERTEX,{"derivedFrom":[subQ1,subQ0]});Q103=makeQuery(id+"F1.imprint","IMPRINT",FACE,{"disambiguationData":[TD([[makeQuery(id+"F1.imprint","IMPRINT",EDGE,{"disambiguationData":[TD([[subQ2,-1.0]])],"derivedFrom":subQ1}),-1.0]])]});}
            var Q104;
            {var subQ0=sQuery(id+"F1.wireOp",EDGE,"E9.15.0");var subQ1=sQuery(id+"F1.wireOp",EDGE,"E9.5.1");var subQ2=makeQuery(id+"F1.imprint","INTERSECT",VERTEX,{"derivedFrom":[subQ1,subQ0]});Q104=makeQuery(id+"F1.imprint","IMPRINT",FACE,{"disambiguationData":[TD([[makeQuery(id+"F1.imprint","IMPRINT",EDGE,{"disambiguationData":[TD([[subQ2,-1.0]])],"derivedFrom":subQ1}),-1.0]])]});}
            var Q105;
            {var subQ0=sQuery(id+"F1.wireOp",EDGE,"E9.11.0");var subQ1=sQuery(id+"F1.wireOp",EDGE,"E6");var subQ2=makeQuery(id+"F1.imprint","INTERSECT",VERTEX,{"derivedFrom":[subQ1,subQ0]});Q105=makeQuery(id+"F1.imprint","IMPRINT",FACE,{"disambiguationData":[TD([[makeQuery(id+"F1.imprint","IMPRINT",EDGE,{"disambiguationData":[TD([[subQ2,-1.0]])],"derivedFrom":subQ1}),-1.0]])]});}
            var Q106;
            {var subQ0=sQuery(id+"F1.wireOp",EDGE,"E9.10.1");var subQ1=sQuery(id+"F1.wireOp",EDGE,"E9.3.0");var subQ2=makeQuery(id+"F1.imprint","INTERSECT",VERTEX,{"derivedFrom":[subQ1,subQ0]});Q106=makeQuery(id+"F1.imprint","IMPRINT",FACE,{"disambiguationData":[TD([[makeQuery(id+"F1.imprint","IMPRINT",EDGE,{"disambiguationData":[TD([[subQ2,-1.0]])],"derivedFrom":subQ1}),1.0]])]});}
            var Q107;
            {var subQ0=sQuery(id+"F1.wireOp",EDGE,"E9.13.1");var subQ1=sQuery(id+"F1.wireOp",EDGE,"E9.5.0");var subQ2=makeQuery(id+"F1.imprint","INTERSECT",VERTEX,{"derivedFrom":[subQ1,subQ0]});Q107=makeQuery(id+"F1.imprint","IMPRINT",FACE,{"disambiguationData":[TD([[makeQuery(id+"F1.imprint","IMPRINT",EDGE,{"disambiguationData":[TD([[subQ2,-1.0]])],"derivedFrom":subQ1}),1.0]])]});}
            var Q108;
            {var subQ0=sQuery(id+"F1.wireOp",EDGE,"E9.12.0");var subQ1=sQuery(id+"F1.wireOp",EDGE,"E9.2.1");var subQ2=makeQuery(id+"F1.imprint","INTERSECT",VERTEX,{"derivedFrom":[subQ1,subQ0]});Q108=makeQuery(id+"F1.imprint","IMPRINT",FACE,{"disambiguationData":[TD([[makeQuery(id+"F1.imprint","IMPRINT",EDGE,{"disambiguationData":[TD([[subQ2,-1.0]])],"derivedFrom":subQ1}),-1.0]])]});}
            var Q109;
            {var subQ0=sQuery(id+"F1.wireOp",EDGE,"E9.8.1");var subQ1=sQuery(id+"F1.wireOp",EDGE,"E9.1.0");var subQ2=makeQuery(id+"F1.imprint","INTERSECT",VERTEX,{"derivedFrom":[subQ1,subQ0]});Q109=makeQuery(id+"F1.imprint","IMPRINT",FACE,{"disambiguationData":[TD([[makeQuery(id+"F1.imprint","IMPRINT",EDGE,{"disambiguationData":[TD([[subQ2,-1.0]])],"derivedFrom":subQ1}),1.0]])]});}
            var Q110;
            {var subQ0=sQuery(id+"F1.wireOp",EDGE,"E9.13.0");var subQ1=sQuery(id+"F1.wireOp",EDGE,"E9.2.1");var subQ2=makeQuery(id+"F1.imprint","INTERSECT",VERTEX,{"derivedFrom":[subQ1,subQ0]});Q110=makeQuery(id+"F1.imprint","IMPRINT",FACE,{"disambiguationData":[TD([[makeQuery(id+"F1.imprint","IMPRINT",EDGE,{"disambiguationData":[TD([[subQ2,-1.0]])],"derivedFrom":subQ1}),-1.0]])]});}
            var Q111;
            {var subQ0=sQuery(id+"F1.wireOp",EDGE,"E9.8.1");var subQ5=sQuery(id+"F1.wireOp",EDGE,"E9.1.0");var subQ6=makeQuery(id+"F1.imprint","INTERSECT",VERTEX,{"derivedFrom":[subQ5,subQ0]});Q111=makeQuery(id+"F1.imprint","IMPRINT",FACE,{"disambiguationData":[TD([[makeQuery(id+"F1.imprint","IMPRINT",EDGE,{"disambiguationData":[TD([[subQ6,-1.0]])],"derivedFrom":subQ5}),-1.0]])]});}
            var Q112;
            {var subQ0=sQuery(id+"F1.wireOp",EDGE,"E9.15.1");var subQ1=sQuery(id+"F1.wireOp",EDGE,"E9.8.0");var subQ2=makeQuery(id+"F1.imprint","INTERSECT",VERTEX,{"derivedFrom":[subQ1,subQ0]});Q112=makeQuery(id+"F1.imprint","IMPRINT",FACE,{"disambiguationData":[TD([[makeQuery(id+"F1.imprint","IMPRINT",EDGE,{"disambiguationData":[TD([[subQ2,-1.0]])],"derivedFrom":subQ1}),1.0]])]});}
            var Q113;
            {var subQ0=sQuery(id+"F1.wireOp",EDGE,"E9.9.1");var subQ1=sQuery(id+"F1.wireOp",EDGE,"E9.1.0");var subQ2=makeQuery(id+"F1.imprint","INTERSECT",VERTEX,{"derivedFrom":[subQ1,subQ0]});Q113=makeQuery(id+"F1.imprint","IMPRINT",FACE,{"disambiguationData":[TD([[makeQuery(id+"F1.imprint","IMPRINT",EDGE,{"disambiguationData":[TD([[subQ2,-1.0]])],"derivedFrom":subQ1}),1.0]])]});}
            var Q114;
            {var subQ0=sQuery(id+"F1.wireOp",EDGE,"E9.10.0");var subQ1=sQuery(id+"F1.wireOp",EDGE,"E6");var subQ2=makeQuery(id+"F1.imprint","INTERSECT",VERTEX,{"derivedFrom":[subQ1,subQ0]});Q114=makeQuery(id+"F1.imprint","IMPRINT",FACE,{"disambiguationData":[TD([[makeQuery(id+"F1.imprint","IMPRINT",EDGE,{"disambiguationData":[TD([[subQ2,-1.0]])],"derivedFrom":subQ1}),1.0]])]});}
            var Q115;
            {var subQ0=sQuery(id+"F1.wireOp",EDGE,"E9.7.1");var subQ1=sQuery(id+"F1.wireOp",EDGE,"E8");var subQ2=makeQuery(id+"F1.imprint","INTERSECT",VERTEX,{"derivedFrom":[subQ1,subQ0]});Q115=makeQuery(id+"F1.imprint","IMPRINT",FACE,{"disambiguationData":[TD([[makeQuery(id+"F1.imprint","IMPRINT",EDGE,{"disambiguationData":[TD([[subQ2,-1.0]])],"derivedFrom":subQ1}),1.0]])]});}
            var Q116;
            {var subQ1=sQuery(id+"F1.wireOp",EDGE,"E6");var subQ3=sQuery(id+"F1.wireOp",EDGE,"E9.9.0");var subQ4=makeQuery(id+"F1.imprint","INTERSECT",VERTEX,{"derivedFrom":[subQ1,subQ3]});Q116=makeQuery(id+"F1.imprint","IMPRINT",FACE,{"disambiguationData":[TD([[makeQuery(id+"F1.imprint","IMPRINT",EDGE,{"disambiguationData":[TD([[subQ4,-1.0]])],"derivedFrom":subQ3}),-1.0]])]});}
            var Q117;
            {var subQ0=sQuery(id+"F1.wireOp",EDGE,"E9.1.1");var subQ1=sQuery(id+"F1.wireOp",EDGE,"E3.0");var subQ2=makeQuery(id+"F1.imprint","INTERSECT",VERTEX,{"derivedFrom":[subQ1,subQ0]});Q117=makeQuery(id+"F1.imprint","IMPRINT",FACE,{"disambiguationData":[TD([[makeQuery(id+"F1.imprint","IMPRINT",EDGE,{"disambiguationData":[TD([[subQ2,-1.0]])],"derivedFrom":subQ1}),1.0]])]});}
            var Q118;
            {var subQ0=sQuery(id+"F1.wireOp",EDGE,"E9.1.1");var subQ1=sQuery(id+"F1.wireOp",EDGE,"E2");var subQ2=makeQuery(id+"F1.imprint","INTERSECT",VERTEX,{"derivedFrom":[subQ1,subQ0]});Q118=makeQuery(id+"F1.imprint","IMPRINT",FACE,{"disambiguationData":[TD([[makeQuery(id+"F1.imprint","IMPRINT",EDGE,{"disambiguationData":[TD([[subQ2,-1.0]])],"derivedFrom":subQ1}),1.0]])]});}
            var Q119;
            {var subQ0=sQuery(id+"F1.wireOp",EDGE,"E9.1.1");var subQ1=sQuery(id+"F1.wireOp",EDGE,"E1.0");var subQ2=makeQuery(id+"F1.imprint","INTERSECT",VERTEX,{"derivedFrom":[subQ1,subQ0]});Q119=makeQuery(id+"F1.imprint","IMPRINT",FACE,{"disambiguationData":[TD([[makeQuery(id+"F1.imprint","IMPRINT",EDGE,{"disambiguationData":[TD([[subQ2,-1.0]])],"derivedFrom":subQ1}),1.0]])]});}
            var Q120;
            {var subQ0=sQuery(id+"F1.wireOp",EDGE,"E6");var subQ1=sQuery(id+"F1.wireOp",EDGE,"E1.0");var subQ2=makeQuery(id+"F1.imprint","INTERSECT",VERTEX,{"derivedFrom":[subQ1,subQ0]});Q120=makeQuery(id+"F1.imprint","IMPRINT",FACE,{"disambiguationData":[TD([[makeQuery(id+"F1.imprint","IMPRINT",EDGE,{"disambiguationData":[TD([[subQ2,-1.0]])],"derivedFrom":subQ1}),1.0]])]});}
            var Q121;
            {var subQ0=sQuery(id+"F1.wireOp",EDGE,"E6");var subQ1=sQuery(id+"F1.wireOp",EDGE,"E2");var subQ2=makeQuery(id+"F1.imprint","INTERSECT",VERTEX,{"derivedFrom":[subQ1,subQ0]});Q121=makeQuery(id+"F1.imprint","IMPRINT",FACE,{"disambiguationData":[TD([[makeQuery(id+"F1.imprint","IMPRINT",EDGE,{"disambiguationData":[TD([[subQ2,-1.0]])],"derivedFrom":subQ1}),1.0]])]});}
            var Q122;
            {var subQ0=sQuery(id+"F1.wireOp",EDGE,"E9.15.1");var subQ1=sQuery(id+"F1.wireOp",EDGE,"E3.0");var subQ2=makeQuery(id+"F1.imprint","INTERSECT",VERTEX,{"derivedFrom":[subQ1,subQ0]});Q122=makeQuery(id+"F1.imprint","IMPRINT",FACE,{"disambiguationData":[TD([[makeQuery(id+"F1.imprint","IMPRINT",EDGE,{"disambiguationData":[TD([[subQ2,-1.0]])],"derivedFrom":subQ1}),1.0]])]});}
            var Q123;
            {var subQ0=sQuery(id+"F1.wireOp",EDGE,"E9.15.1");var subQ1=sQuery(id+"F1.wireOp",EDGE,"E2");var subQ2=makeQuery(id+"F1.imprint","INTERSECT",VERTEX,{"derivedFrom":[subQ1,subQ0]});Q123=makeQuery(id+"F1.imprint","IMPRINT",FACE,{"disambiguationData":[TD([[makeQuery(id+"F1.imprint","IMPRINT",EDGE,{"disambiguationData":[TD([[subQ2,-1.0]])],"derivedFrom":subQ1}),1.0]])]});}
            var Q124;
            {var subQ0=sQuery(id+"F1.wireOp",EDGE,"E9.14.1");var subQ1=sQuery(id+"F1.wireOp",EDGE,"E2");var subQ2=makeQuery(id+"F1.imprint","INTERSECT",VERTEX,{"derivedFrom":[subQ1,subQ0]});Q124=makeQuery(id+"F1.imprint","IMPRINT",FACE,{"disambiguationData":[TD([[makeQuery(id+"F1.imprint","IMPRINT",EDGE,{"disambiguationData":[TD([[subQ2,-1.0]])],"derivedFrom":subQ1}),1.0]])]});}
            var Q125;
            {var subQ0=sQuery(id+"F1.wireOp",EDGE,"E9.14.1");var subQ1=sQuery(id+"F1.wireOp",EDGE,"E3.0");var subQ2=makeQuery(id+"F1.imprint","INTERSECT",VERTEX,{"derivedFrom":[subQ1,subQ0]});Q125=makeQuery(id+"F1.imprint","IMPRINT",FACE,{"disambiguationData":[TD([[makeQuery(id+"F1.imprint","IMPRINT",EDGE,{"disambiguationData":[TD([[subQ2,-1.0]])],"derivedFrom":subQ1}),1.0]])]});}
            var Q126;
            {var subQ0=sQuery(id+"F1.wireOp",EDGE,"E9.13.1");var subQ1=sQuery(id+"F1.wireOp",EDGE,"E2");var subQ2=makeQuery(id+"F1.imprint","INTERSECT",VERTEX,{"derivedFrom":[subQ1,subQ0]});Q126=makeQuery(id+"F1.imprint","IMPRINT",FACE,{"disambiguationData":[TD([[makeQuery(id+"F1.imprint","IMPRINT",EDGE,{"disambiguationData":[TD([[subQ2,-1.0]])],"derivedFrom":subQ1}),1.0]])]});}
            var Q127;
            {var subQ0=sQuery(id+"F1.wireOp",EDGE,"E9.13.1");var subQ1=sQuery(id+"F1.wireOp",EDGE,"E1.0");var subQ2=makeQuery(id+"F1.imprint","INTERSECT",VERTEX,{"derivedFrom":[subQ1,subQ0]});Q127=makeQuery(id+"F1.imprint","IMPRINT",FACE,{"disambiguationData":[TD([[makeQuery(id+"F1.imprint","IMPRINT",EDGE,{"disambiguationData":[TD([[subQ2,-1.0]])],"derivedFrom":subQ1}),1.0]])]});}
            var Q128;
            {var subQ0=sQuery(id+"F1.wireOp",EDGE,"E9.13.1");var subQ1=sQuery(id+"F1.wireOp",EDGE,"E3.0");var subQ2=makeQuery(id+"F1.imprint","INTERSECT",VERTEX,{"derivedFrom":[subQ1,subQ0]});Q128=makeQuery(id+"F1.imprint","IMPRINT",FACE,{"disambiguationData":[TD([[makeQuery(id+"F1.imprint","IMPRINT",EDGE,{"disambiguationData":[TD([[subQ2,-1.0]])],"derivedFrom":subQ1}),1.0]])]});}
            var Q129;
            {var subQ0=sQuery(id+"F1.wireOp",EDGE,"E9.12.0");var subQ1=sQuery(id+"F1.wireOp",EDGE,"E2");var subQ2=makeQuery(id+"F1.imprint","INTERSECT",VERTEX,{"derivedFrom":[subQ1,subQ0]});Q129=makeQuery(id+"F1.imprint","IMPRINT",FACE,{"disambiguationData":[TD([[makeQuery(id+"F1.imprint","IMPRINT",EDGE,{"disambiguationData":[TD([[subQ2,1.0]])],"derivedFrom":subQ1}),1.0]])]});}
            var Q130;
            {var subQ0=sQuery(id+"F1.wireOp",EDGE,"E9.12.0");var subQ1=sQuery(id+"F1.wireOp",EDGE,"E1.0");var subQ2=makeQuery(id+"F1.imprint","INTERSECT",VERTEX,{"derivedFrom":[subQ1,subQ0]});Q130=makeQuery(id+"F1.imprint","IMPRINT",FACE,{"disambiguationData":[TD([[makeQuery(id+"F1.imprint","IMPRINT",EDGE,{"disambiguationData":[TD([[subQ2,1.0]])],"derivedFrom":subQ1}),1.0]])]});}
            var Q131;
            {var subQ0=sQuery(id+"F1.wireOp",EDGE,"E9.12.0");var subQ1=sQuery(id+"F1.wireOp",EDGE,"E3.0");var subQ2=makeQuery(id+"F1.imprint","INTERSECT",VERTEX,{"derivedFrom":[subQ1,subQ0]});Q131=makeQuery(id+"F1.imprint","IMPRINT",FACE,{"disambiguationData":[TD([[makeQuery(id+"F1.imprint","IMPRINT",EDGE,{"disambiguationData":[TD([[subQ2,1.0]])],"derivedFrom":subQ1}),1.0]])]});}
            var Q132;
            {var subQ0=sQuery(id+"F1.wireOp",EDGE,"E9.11.1");var subQ1=sQuery(id+"F1.wireOp",EDGE,"E3.0");var subQ2=makeQuery(id+"F1.imprint","INTERSECT",VERTEX,{"derivedFrom":[subQ1,subQ0]});Q132=makeQuery(id+"F1.imprint","IMPRINT",FACE,{"disambiguationData":[TD([[makeQuery(id+"F1.imprint","IMPRINT",EDGE,{"disambiguationData":[TD([[subQ2,-1.0]])],"derivedFrom":subQ1}),1.0]])]});}
            var Q133;
            {var subQ0=sQuery(id+"F1.wireOp",EDGE,"E9.11.1");var subQ1=sQuery(id+"F1.wireOp",EDGE,"E2");var subQ2=makeQuery(id+"F1.imprint","INTERSECT",VERTEX,{"derivedFrom":[subQ1,subQ0]});Q133=makeQuery(id+"F1.imprint","IMPRINT",FACE,{"disambiguationData":[TD([[makeQuery(id+"F1.imprint","IMPRINT",EDGE,{"disambiguationData":[TD([[subQ2,-1.0]])],"derivedFrom":subQ1}),1.0]])]});}
            var Q134;
            {var subQ0=sQuery(id+"F1.wireOp",EDGE,"E9.11.1");var subQ1=sQuery(id+"F1.wireOp",EDGE,"E1.0");var subQ2=makeQuery(id+"F1.imprint","INTERSECT",VERTEX,{"derivedFrom":[subQ1,subQ0]});Q134=makeQuery(id+"F1.imprint","IMPRINT",FACE,{"disambiguationData":[TD([[makeQuery(id+"F1.imprint","IMPRINT",EDGE,{"disambiguationData":[TD([[subQ2,-1.0]])],"derivedFrom":subQ1}),1.0]])]});}
            var Q135;
            {var subQ0=sQuery(id+"F1.wireOp",EDGE,"E9.10.1");var subQ1=sQuery(id+"F1.wireOp",EDGE,"E1.0");var subQ2=makeQuery(id+"F1.imprint","INTERSECT",VERTEX,{"derivedFrom":[subQ1,subQ0]});Q135=makeQuery(id+"F1.imprint","IMPRINT",FACE,{"disambiguationData":[TD([[makeQuery(id+"F1.imprint","IMPRINT",EDGE,{"disambiguationData":[TD([[subQ2,-1.0]])],"derivedFrom":subQ1}),1.0]])]});}
            var Q136;
            {var subQ0=sQuery(id+"F1.wireOp",EDGE,"E9.10.1");var subQ1=sQuery(id+"F1.wireOp",EDGE,"E2");var subQ2=makeQuery(id+"F1.imprint","INTERSECT",VERTEX,{"derivedFrom":[subQ1,subQ0]});Q136=makeQuery(id+"F1.imprint","IMPRINT",FACE,{"disambiguationData":[TD([[makeQuery(id+"F1.imprint","IMPRINT",EDGE,{"disambiguationData":[TD([[subQ2,-1.0]])],"derivedFrom":subQ1}),1.0]])]});}
            var Q137;
            {var subQ0=sQuery(id+"F1.wireOp",EDGE,"E9.10.1");var subQ1=sQuery(id+"F1.wireOp",EDGE,"E3.0");var subQ2=makeQuery(id+"F1.imprint","INTERSECT",VERTEX,{"derivedFrom":[subQ1,subQ0]});Q137=makeQuery(id+"F1.imprint","IMPRINT",FACE,{"disambiguationData":[TD([[makeQuery(id+"F1.imprint","IMPRINT",EDGE,{"disambiguationData":[TD([[subQ2,-1.0]])],"derivedFrom":subQ1}),1.0]])]});}
            var Q138;
            {var subQ0=sQuery(id+"F1.wireOp",EDGE,"E9.9.1");var subQ1=sQuery(id+"F1.wireOp",EDGE,"E3.0");var subQ2=makeQuery(id+"F1.imprint","INTERSECT",VERTEX,{"derivedFrom":[subQ1,subQ0]});Q138=makeQuery(id+"F1.imprint","IMPRINT",FACE,{"disambiguationData":[TD([[makeQuery(id+"F1.imprint","IMPRINT",EDGE,{"disambiguationData":[TD([[subQ2,-1.0]])],"derivedFrom":subQ1}),1.0]])]});}
            var Q139;
            {var subQ0=sQuery(id+"F1.wireOp",EDGE,"E9.9.1");var subQ1=sQuery(id+"F1.wireOp",EDGE,"E2");var subQ2=makeQuery(id+"F1.imprint","INTERSECT",VERTEX,{"derivedFrom":[subQ1,subQ0]});Q139=makeQuery(id+"F1.imprint","IMPRINT",FACE,{"disambiguationData":[TD([[makeQuery(id+"F1.imprint","IMPRINT",EDGE,{"disambiguationData":[TD([[subQ2,-1.0]])],"derivedFrom":subQ1}),1.0]])]});}
            var Q140;
            {var subQ0=sQuery(id+"F1.wireOp",EDGE,"E9.9.1");var subQ1=sQuery(id+"F1.wireOp",EDGE,"E1.0");var subQ2=makeQuery(id+"F1.imprint","INTERSECT",VERTEX,{"derivedFrom":[subQ1,subQ0]});Q140=makeQuery(id+"F1.imprint","IMPRINT",FACE,{"disambiguationData":[TD([[makeQuery(id+"F1.imprint","IMPRINT",EDGE,{"disambiguationData":[TD([[subQ2,-1.0]])],"derivedFrom":subQ1}),1.0]])]});}
            var Q141;
            {var subQ0=sQuery(id+"F1.wireOp",EDGE,"E9.8.1");var subQ1=sQuery(id+"F1.wireOp",EDGE,"E1.0");var subQ2=makeQuery(id+"F1.imprint","INTERSECT",VERTEX,{"derivedFrom":[subQ1,subQ0]});Q141=makeQuery(id+"F1.imprint","IMPRINT",FACE,{"disambiguationData":[TD([[makeQuery(id+"F1.imprint","IMPRINT",EDGE,{"disambiguationData":[TD([[subQ2,-1.0]])],"derivedFrom":subQ1}),1.0]])]});}
            var Q142;
            {var subQ0=sQuery(id+"F1.wireOp",EDGE,"E9.8.1");var subQ1=sQuery(id+"F1.wireOp",EDGE,"E2");var subQ2=makeQuery(id+"F1.imprint","INTERSECT",VERTEX,{"derivedFrom":[subQ1,subQ0]});Q142=makeQuery(id+"F1.imprint","IMPRINT",FACE,{"disambiguationData":[TD([[makeQuery(id+"F1.imprint","IMPRINT",EDGE,{"disambiguationData":[TD([[subQ2,-1.0]])],"derivedFrom":subQ1}),1.0]])]});}
            var Q143;
            {var subQ0=sQuery(id+"F1.wireOp",EDGE,"E9.8.1");var subQ1=sQuery(id+"F1.wireOp",EDGE,"E3.0");var subQ2=makeQuery(id+"F1.imprint","INTERSECT",VERTEX,{"derivedFrom":[subQ1,subQ0]});Q143=makeQuery(id+"F1.imprint","IMPRINT",FACE,{"disambiguationData":[TD([[makeQuery(id+"F1.imprint","IMPRINT",EDGE,{"disambiguationData":[TD([[subQ2,-1.0]])],"derivedFrom":subQ1}),1.0]])]});}
            var Q144;
            {var subQ0=sQuery(id+"F1.wireOp",EDGE,"E9.7.1");var subQ1=sQuery(id+"F1.wireOp",EDGE,"E3.0");var subQ2=makeQuery(id+"F1.imprint","INTERSECT",VERTEX,{"derivedFrom":[subQ1,subQ0]});Q144=makeQuery(id+"F1.imprint","IMPRINT",FACE,{"disambiguationData":[TD([[makeQuery(id+"F1.imprint","IMPRINT",EDGE,{"disambiguationData":[TD([[subQ2,-1.0]])],"derivedFrom":subQ1}),1.0]])]});}
            var Q145;
            {var subQ0=sQuery(id+"F1.wireOp",EDGE,"E9.7.1");var subQ1=sQuery(id+"F1.wireOp",EDGE,"E2");var subQ2=makeQuery(id+"F1.imprint","INTERSECT",VERTEX,{"derivedFrom":[subQ1,subQ0]});Q145=makeQuery(id+"F1.imprint","IMPRINT",FACE,{"disambiguationData":[TD([[makeQuery(id+"F1.imprint","IMPRINT",EDGE,{"disambiguationData":[TD([[subQ2,-1.0]])],"derivedFrom":subQ1}),1.0]])]});}
            var Q146;
            {var subQ0=sQuery(id+"F1.wireOp",EDGE,"E9.7.0");var subQ1=sQuery(id+"F1.wireOp",EDGE,"E0");var subQ2=makeQuery(id+"F1.imprint","INTERSECT",VERTEX,{"derivedFrom":[subQ1,subQ0]});Q146=makeQuery(id+"F1.imprint","IMPRINT",FACE,{"disambiguationData":[TD([[makeQuery(id+"F1.imprint","IMPRINT",EDGE,{"disambiguationData":[TD([[subQ2,1.0]])],"derivedFrom":subQ1}),1.0]])]});}
            var Q147;
            {var subQ0=sQuery(id+"F1.wireOp",EDGE,"E9.6.0");var subQ1=sQuery(id+"F1.wireOp",EDGE,"E0");var subQ2=makeQuery(id+"F1.imprint","INTERSECT",VERTEX,{"derivedFrom":[subQ1,subQ0]});Q147=makeQuery(id+"F1.imprint","IMPRINT",FACE,{"disambiguationData":[TD([[makeQuery(id+"F1.imprint","IMPRINT",EDGE,{"disambiguationData":[TD([[subQ2,1.0]])],"derivedFrom":subQ1}),1.0]])]});}
            var Q148;
            {var subQ0=sQuery(id+"F1.wireOp",EDGE,"E9.6.1");var subQ1=sQuery(id+"F1.wireOp",EDGE,"E1.0");var subQ2=makeQuery(id+"F1.imprint","INTERSECT",VERTEX,{"derivedFrom":[subQ1,subQ0]});Q148=makeQuery(id+"F1.imprint","IMPRINT",FACE,{"disambiguationData":[TD([[makeQuery(id+"F1.imprint","IMPRINT",EDGE,{"disambiguationData":[TD([[subQ2,-1.0]])],"derivedFrom":subQ1}),1.0]])]});}
            var Q149;
            {var subQ0=sQuery(id+"F1.wireOp",EDGE,"E9.6.1");var subQ1=sQuery(id+"F1.wireOp",EDGE,"E2");var subQ2=makeQuery(id+"F1.imprint","INTERSECT",VERTEX,{"derivedFrom":[subQ1,subQ0]});Q149=makeQuery(id+"F1.imprint","IMPRINT",FACE,{"disambiguationData":[TD([[makeQuery(id+"F1.imprint","IMPRINT",EDGE,{"disambiguationData":[TD([[subQ2,-1.0]])],"derivedFrom":subQ1}),1.0]])]});}
            var Q150;
            {var subQ0=sQuery(id+"F1.wireOp",EDGE,"E9.6.1");var subQ1=sQuery(id+"F1.wireOp",EDGE,"E3.0");var subQ2=makeQuery(id+"F1.imprint","INTERSECT",VERTEX,{"derivedFrom":[subQ1,subQ0]});Q150=makeQuery(id+"F1.imprint","IMPRINT",FACE,{"disambiguationData":[TD([[makeQuery(id+"F1.imprint","IMPRINT",EDGE,{"disambiguationData":[TD([[subQ2,-1.0]])],"derivedFrom":subQ1}),1.0]])]});}
            var Q151;
            {var subQ0=sQuery(id+"F1.wireOp",EDGE,"E9.5.0");var subQ1=sQuery(id+"F1.wireOp",EDGE,"E2");var subQ2=makeQuery(id+"F1.imprint","INTERSECT",VERTEX,{"derivedFrom":[subQ1,subQ0]});Q151=makeQuery(id+"F1.imprint","IMPRINT",FACE,{"disambiguationData":[TD([[makeQuery(id+"F1.imprint","IMPRINT",EDGE,{"disambiguationData":[TD([[subQ2,-1.0]])],"derivedFrom":subQ1}),1.0]])]});}
            var Q152;
            {var subQ0=sQuery(id+"F1.wireOp",EDGE,"E9.5.1");var subQ1=sQuery(id+"F1.wireOp",EDGE,"E2");var subQ2=makeQuery(id+"F1.imprint","INTERSECT",VERTEX,{"derivedFrom":[subQ1,subQ0]});Q152=makeQuery(id+"F1.imprint","IMPRINT",FACE,{"disambiguationData":[TD([[makeQuery(id+"F1.imprint","IMPRINT",EDGE,{"disambiguationData":[TD([[subQ2,-1.0]])],"derivedFrom":subQ1}),1.0]])]});}
            var Q153;
            {var subQ0=sQuery(id+"F1.wireOp",EDGE,"E9.4.0");var subQ1=sQuery(id+"F1.wireOp",EDGE,"E2");var subQ2=makeQuery(id+"F1.imprint","INTERSECT",VERTEX,{"derivedFrom":[subQ1,subQ0]});Q153=makeQuery(id+"F1.imprint","IMPRINT",FACE,{"disambiguationData":[TD([[makeQuery(id+"F1.imprint","IMPRINT",EDGE,{"disambiguationData":[TD([[subQ2,-1.0]])],"derivedFrom":subQ1}),1.0]])]});}
            var Q154;
            {var subQ0=sQuery(id+"F1.wireOp",EDGE,"E9.4.1");var subQ1=sQuery(id+"F1.wireOp",EDGE,"E2");var subQ2=makeQuery(id+"F1.imprint","INTERSECT",VERTEX,{"derivedFrom":[subQ1,subQ0]});Q154=makeQuery(id+"F1.imprint","IMPRINT",FACE,{"disambiguationData":[TD([[makeQuery(id+"F1.imprint","IMPRINT",EDGE,{"disambiguationData":[TD([[subQ2,-1.0]])],"derivedFrom":subQ1}),1.0]])]});}
            var Q155;
            {var subQ0=sQuery(id+"F1.wireOp",EDGE,"E9.3.0");var subQ1=sQuery(id+"F1.wireOp",EDGE,"E2");var subQ2=makeQuery(id+"F1.imprint","INTERSECT",VERTEX,{"derivedFrom":[subQ1,subQ0]});Q155=makeQuery(id+"F1.imprint","IMPRINT",FACE,{"disambiguationData":[TD([[makeQuery(id+"F1.imprint","IMPRINT",EDGE,{"disambiguationData":[TD([[subQ2,-1.0]])],"derivedFrom":subQ1}),1.0]])]});}
            var Q156;
            {var subQ0=sQuery(id+"F1.wireOp",EDGE,"E9.3.1");var subQ1=sQuery(id+"F1.wireOp",EDGE,"E2");var subQ2=makeQuery(id+"F1.imprint","INTERSECT",VERTEX,{"derivedFrom":[subQ1,subQ0]});Q156=makeQuery(id+"F1.imprint","IMPRINT",FACE,{"disambiguationData":[TD([[makeQuery(id+"F1.imprint","IMPRINT",EDGE,{"disambiguationData":[TD([[subQ2,-1.0]])],"derivedFrom":subQ1}),1.0]])]});}
            var Q157;
            {var subQ0=sQuery(id+"F1.wireOp",EDGE,"E9.2.0");var subQ1=sQuery(id+"F1.wireOp",EDGE,"E2");var subQ2=makeQuery(id+"F1.imprint","INTERSECT",VERTEX,{"derivedFrom":[subQ1,subQ0]});Q157=makeQuery(id+"F1.imprint","IMPRINT",FACE,{"disambiguationData":[TD([[makeQuery(id+"F1.imprint","IMPRINT",EDGE,{"disambiguationData":[TD([[subQ2,-1.0]])],"derivedFrom":subQ1}),1.0]])]});}
            var Q158;
            {var subQ0=sQuery(id+"F1.wireOp",EDGE,"E9.1.0");var subQ1=sQuery(id+"F1.wireOp",EDGE,"E2");var subQ2=makeQuery(id+"F1.imprint","INTERSECT",VERTEX,{"derivedFrom":[subQ1,subQ0]});Q158=makeQuery(id+"F1.imprint","IMPRINT",FACE,{"disambiguationData":[TD([[makeQuery(id+"F1.imprint","IMPRINT",EDGE,{"disambiguationData":[TD([[subQ2,-1.0]])],"derivedFrom":subQ1}),1.0]])]});}
            var Q159;
            {var subQ0=sQuery(id+"F1.wireOp",EDGE,"E8");var subQ1=sQuery(id+"F1.wireOp",EDGE,"E2");var subQ2=makeQuery(id+"F1.imprint","INTERSECT",VERTEX,{"derivedFrom":[subQ1,subQ0]});Q159=makeQuery(id+"F1.imprint","IMPRINT",FACE,{"disambiguationData":[TD([[makeQuery(id+"F1.imprint","IMPRINT",EDGE,{"disambiguationData":[TD([[subQ2,-1.0]])],"derivedFrom":subQ1}),1.0]])]});}
            var Q160;
            {var subQ0=sQuery(id+"F1.wireOp",EDGE,"E9.15.0");var subQ1=sQuery(id+"F1.wireOp",EDGE,"E2");var subQ2=makeQuery(id+"F1.imprint","INTERSECT",VERTEX,{"derivedFrom":[subQ1,subQ0]});Q160=makeQuery(id+"F1.imprint","IMPRINT",FACE,{"disambiguationData":[TD([[makeQuery(id+"F1.imprint","IMPRINT",EDGE,{"disambiguationData":[TD([[subQ2,-1.0]])],"derivedFrom":subQ1}),1.0]])]});}
            var Q161;
            {var subQ0=sQuery(id+"F1.wireOp",EDGE,"E6");var subQ1=sQuery(id+"F1.wireOp",EDGE,"E3.0");var subQ2=makeQuery(id+"F1.imprint","INTERSECT",VERTEX,{"derivedFrom":[subQ1,subQ0]});Q161=makeQuery(id+"F1.imprint","IMPRINT",FACE,{"disambiguationData":[TD([[makeQuery(id+"F1.imprint","IMPRINT",EDGE,{"disambiguationData":[TD([[subQ2,-1.0]])],"derivedFrom":subQ1}),1.0]])]});}
            var Q162;
            {var subQ0=sQuery(id+"F1.wireOp",EDGE,"E9.15.1");var subQ1=sQuery(id+"F1.wireOp",EDGE,"E1.0");var subQ2=makeQuery(id+"F1.imprint","INTERSECT",VERTEX,{"derivedFrom":[subQ1,subQ0]});Q162=makeQuery(id+"F1.imprint","IMPRINT",FACE,{"disambiguationData":[TD([[makeQuery(id+"F1.imprint","IMPRINT",EDGE,{"disambiguationData":[TD([[subQ2,-1.0]])],"derivedFrom":subQ1}),1.0]])]});}
            var Q163;
            {var subQ0=sQuery(id+"F1.wireOp",EDGE,"E9.14.1");var subQ1=sQuery(id+"F1.wireOp",EDGE,"E1.0");var subQ2=makeQuery(id+"F1.imprint","INTERSECT",VERTEX,{"derivedFrom":[subQ1,subQ0]});Q163=makeQuery(id+"F1.imprint","IMPRINT",FACE,{"disambiguationData":[TD([[makeQuery(id+"F1.imprint","IMPRINT",EDGE,{"disambiguationData":[TD([[subQ2,-1.0]])],"derivedFrom":subQ1}),1.0]])]});}
            var Q164;
            {var subQ0=sQuery(id+"F1.wireOp",EDGE,"E9.14.0");var subQ1=sQuery(id+"F1.wireOp",EDGE,"E0");var subQ2=makeQuery(id+"F1.imprint","INTERSECT",VERTEX,{"derivedFrom":[subQ1,subQ0]});Q164=makeQuery(id+"F1.imprint","IMPRINT",FACE,{"disambiguationData":[TD([[makeQuery(id+"F1.imprint","IMPRINT",EDGE,{"disambiguationData":[TD([[subQ2,1.0]])],"derivedFrom":subQ1}),1.0]])]});}
            var Q165;
            {var subQ0=sQuery(id+"F1.wireOp",EDGE,"E9.13.0");var subQ1=sQuery(id+"F1.wireOp",EDGE,"E0");var subQ2=makeQuery(id+"F1.imprint","INTERSECT",VERTEX,{"derivedFrom":[subQ1,subQ0]});Q165=makeQuery(id+"F1.imprint","IMPRINT",FACE,{"disambiguationData":[TD([[makeQuery(id+"F1.imprint","IMPRINT",EDGE,{"disambiguationData":[TD([[subQ2,-1.0]])],"derivedFrom":subQ1}),1.0]])]});}
            var Q166;
            {var subQ0=sQuery(id+"F1.wireOp",EDGE,"E9.13.0");var subQ1=sQuery(id+"F1.wireOp",EDGE,"E0");var subQ2=makeQuery(id+"F1.imprint","INTERSECT",VERTEX,{"derivedFrom":[subQ1,subQ0]});Q166=makeQuery(id+"F1.imprint","IMPRINT",FACE,{"disambiguationData":[TD([[makeQuery(id+"F1.imprint","IMPRINT",EDGE,{"disambiguationData":[TD([[subQ2,1.0]])],"derivedFrom":subQ1}),1.0]])]});}
            var Q167;
            {var subQ0=sQuery(id+"F1.wireOp",EDGE,"E9.12.0");var subQ1=sQuery(id+"F1.wireOp",EDGE,"E0");var subQ2=makeQuery(id+"F1.imprint","INTERSECT",VERTEX,{"derivedFrom":[subQ1,subQ0]});Q167=makeQuery(id+"F1.imprint","IMPRINT",FACE,{"disambiguationData":[TD([[makeQuery(id+"F1.imprint","IMPRINT",EDGE,{"disambiguationData":[TD([[subQ2,-1.0]])],"derivedFrom":subQ1}),1.0]])]});}
            var Q168;
            {var subQ0=sQuery(id+"F1.wireOp",EDGE,"E9.12.0");var subQ1=sQuery(id+"F1.wireOp",EDGE,"E0");var subQ2=makeQuery(id+"F1.imprint","INTERSECT",VERTEX,{"derivedFrom":[subQ1,subQ0]});Q168=makeQuery(id+"F1.imprint","IMPRINT",FACE,{"disambiguationData":[TD([[makeQuery(id+"F1.imprint","IMPRINT",EDGE,{"disambiguationData":[TD([[subQ2,1.0]])],"derivedFrom":subQ1}),1.0]])]});}
            var Q169;
            {var subQ0=sQuery(id+"F1.wireOp",EDGE,"E9.11.0");var subQ1=sQuery(id+"F1.wireOp",EDGE,"E0");var subQ2=makeQuery(id+"F1.imprint","INTERSECT",VERTEX,{"derivedFrom":[subQ1,subQ0]});Q169=makeQuery(id+"F1.imprint","IMPRINT",FACE,{"disambiguationData":[TD([[makeQuery(id+"F1.imprint","IMPRINT",EDGE,{"disambiguationData":[TD([[subQ2,-1.0]])],"derivedFrom":subQ1}),1.0]])]});}
            var Q170;
            {var subQ0=sQuery(id+"F1.wireOp",EDGE,"E9.11.0");var subQ1=sQuery(id+"F1.wireOp",EDGE,"E0");var subQ2=makeQuery(id+"F1.imprint","INTERSECT",VERTEX,{"derivedFrom":[subQ1,subQ0]});Q170=makeQuery(id+"F1.imprint","IMPRINT",FACE,{"disambiguationData":[TD([[makeQuery(id+"F1.imprint","IMPRINT",EDGE,{"disambiguationData":[TD([[subQ2,1.0]])],"derivedFrom":subQ1}),1.0]])]});}
            var Q171;
            {var subQ0=sQuery(id+"F1.wireOp",EDGE,"E9.10.0");var subQ1=sQuery(id+"F1.wireOp",EDGE,"E0");var subQ2=makeQuery(id+"F1.imprint","INTERSECT",VERTEX,{"derivedFrom":[subQ1,subQ0]});Q171=makeQuery(id+"F1.imprint","IMPRINT",FACE,{"disambiguationData":[TD([[makeQuery(id+"F1.imprint","IMPRINT",EDGE,{"disambiguationData":[TD([[subQ2,-1.0]])],"derivedFrom":subQ1}),1.0]])]});}
            var Q172;
            {var subQ0=sQuery(id+"F1.wireOp",EDGE,"E9.10.0");var subQ1=sQuery(id+"F1.wireOp",EDGE,"E0");var subQ2=makeQuery(id+"F1.imprint","INTERSECT",VERTEX,{"derivedFrom":[subQ1,subQ0]});Q172=makeQuery(id+"F1.imprint","IMPRINT",FACE,{"disambiguationData":[TD([[makeQuery(id+"F1.imprint","IMPRINT",EDGE,{"disambiguationData":[TD([[subQ2,1.0]])],"derivedFrom":subQ1}),1.0]])]});}
            var Q173;
            {var subQ0=sQuery(id+"F1.wireOp",EDGE,"E9.9.0");var subQ1=sQuery(id+"F1.wireOp",EDGE,"E0");var subQ2=makeQuery(id+"F1.imprint","INTERSECT",VERTEX,{"derivedFrom":[subQ1,subQ0]});Q173=makeQuery(id+"F1.imprint","IMPRINT",FACE,{"disambiguationData":[TD([[makeQuery(id+"F1.imprint","IMPRINT",EDGE,{"disambiguationData":[TD([[subQ2,-1.0]])],"derivedFrom":subQ1}),1.0]])]});}
            var Q174;
            {var subQ0=sQuery(id+"F1.wireOp",EDGE,"E9.9.0");var subQ1=sQuery(id+"F1.wireOp",EDGE,"E0");var subQ2=makeQuery(id+"F1.imprint","INTERSECT",VERTEX,{"derivedFrom":[subQ1,subQ0]});Q174=makeQuery(id+"F1.imprint","IMPRINT",FACE,{"disambiguationData":[TD([[makeQuery(id+"F1.imprint","IMPRINT",EDGE,{"disambiguationData":[TD([[subQ2,1.0]])],"derivedFrom":subQ1}),1.0]])]});}
            var Q175;
            {var subQ0=sQuery(id+"F1.wireOp",EDGE,"E9.8.0");var subQ1=sQuery(id+"F1.wireOp",EDGE,"E0");var subQ2=makeQuery(id+"F1.imprint","INTERSECT",VERTEX,{"derivedFrom":[subQ1,subQ0]});Q175=makeQuery(id+"F1.imprint","IMPRINT",FACE,{"disambiguationData":[TD([[makeQuery(id+"F1.imprint","IMPRINT",EDGE,{"disambiguationData":[TD([[subQ2,-1.0]])],"derivedFrom":subQ1}),1.0]])]});}
            var Q176;
            {var subQ0=sQuery(id+"F1.wireOp",EDGE,"E9.8.0");var subQ1=sQuery(id+"F1.wireOp",EDGE,"E0");var subQ2=makeQuery(id+"F1.imprint","INTERSECT",VERTEX,{"derivedFrom":[subQ1,subQ0]});Q176=makeQuery(id+"F1.imprint","IMPRINT",FACE,{"disambiguationData":[TD([[makeQuery(id+"F1.imprint","IMPRINT",EDGE,{"disambiguationData":[TD([[subQ2,1.0]])],"derivedFrom":subQ1}),1.0]])]});}
            var Q177;
            {var subQ0=sQuery(id+"F1.wireOp",EDGE,"E9.7.0");var subQ1=sQuery(id+"F1.wireOp",EDGE,"E0");var subQ2=makeQuery(id+"F1.imprint","INTERSECT",VERTEX,{"derivedFrom":[subQ1,subQ0]});Q177=makeQuery(id+"F1.imprint","IMPRINT",FACE,{"disambiguationData":[TD([[makeQuery(id+"F1.imprint","IMPRINT",EDGE,{"disambiguationData":[TD([[subQ2,-1.0]])],"derivedFrom":subQ1}),1.0]])]});}
            var Q178;
            {var subQ0=sQuery(id+"F1.wireOp",EDGE,"E9.7.1");var subQ1=sQuery(id+"F1.wireOp",EDGE,"E1.0");var subQ2=makeQuery(id+"F1.imprint","INTERSECT",VERTEX,{"derivedFrom":[subQ1,subQ0]});Q178=makeQuery(id+"F1.imprint","IMPRINT",FACE,{"disambiguationData":[TD([[makeQuery(id+"F1.imprint","IMPRINT",EDGE,{"disambiguationData":[TD([[subQ2,-1.0]])],"derivedFrom":subQ1}),1.0]])]});}
            var Q179;
            {var subQ0=sQuery(id+"F1.wireOp",EDGE,"E9.6.0");var subQ1=sQuery(id+"F1.wireOp",EDGE,"E0");var subQ2=makeQuery(id+"F1.imprint","INTERSECT",VERTEX,{"derivedFrom":[subQ1,subQ0]});Q179=makeQuery(id+"F1.imprint","IMPRINT",FACE,{"disambiguationData":[TD([[makeQuery(id+"F1.imprint","IMPRINT",EDGE,{"disambiguationData":[TD([[subQ2,-1.0]])],"derivedFrom":subQ1}),1.0]])]});}
            var Q180;
            {var subQ0=sQuery(id+"F1.wireOp",EDGE,"E9.5.0");var subQ1=sQuery(id+"F1.wireOp",EDGE,"E0");var subQ2=makeQuery(id+"F1.imprint","INTERSECT",VERTEX,{"derivedFrom":[subQ1,subQ0]});Q180=makeQuery(id+"F1.imprint","IMPRINT",FACE,{"disambiguationData":[TD([[makeQuery(id+"F1.imprint","IMPRINT",EDGE,{"disambiguationData":[TD([[subQ2,-1.0]])],"derivedFrom":subQ1}),1.0]])]});}
            var Q181;
            {var subQ0=sQuery(id+"F1.wireOp",EDGE,"E9.5.0");var subQ1=sQuery(id+"F1.wireOp",EDGE,"E0");var subQ2=makeQuery(id+"F1.imprint","INTERSECT",VERTEX,{"derivedFrom":[subQ1,subQ0]});Q181=makeQuery(id+"F1.imprint","IMPRINT",FACE,{"disambiguationData":[TD([[makeQuery(id+"F1.imprint","IMPRINT",EDGE,{"disambiguationData":[TD([[subQ2,1.0]])],"derivedFrom":subQ1}),1.0]])]});}
            var Q182;
            {var subQ0=sQuery(id+"F1.wireOp",EDGE,"E9.5.1");var subQ1=sQuery(id+"F1.wireOp",EDGE,"E1.0");var subQ2=makeQuery(id+"F1.imprint","INTERSECT",VERTEX,{"derivedFrom":[subQ1,subQ0]});Q182=makeQuery(id+"F1.imprint","IMPRINT",FACE,{"disambiguationData":[TD([[makeQuery(id+"F1.imprint","IMPRINT",EDGE,{"disambiguationData":[TD([[subQ2,-1.0]])],"derivedFrom":subQ1}),1.0]])]});}
            var Q183;
            {var subQ0=sQuery(id+"F1.wireOp",EDGE,"E9.4.1");var subQ1=sQuery(id+"F1.wireOp",EDGE,"E1.0");var subQ2=makeQuery(id+"F1.imprint","INTERSECT",VERTEX,{"derivedFrom":[subQ1,subQ0]});Q183=makeQuery(id+"F1.imprint","IMPRINT",FACE,{"disambiguationData":[TD([[makeQuery(id+"F1.imprint","IMPRINT",EDGE,{"disambiguationData":[TD([[subQ2,-1.0]])],"derivedFrom":subQ1}),1.0]])]});}
            var Q184;
            {var subQ0=sQuery(id+"F1.wireOp",EDGE,"E9.4.0");var subQ1=sQuery(id+"F1.wireOp",EDGE,"E0");var subQ2=makeQuery(id+"F1.imprint","INTERSECT",VERTEX,{"derivedFrom":[subQ1,subQ0]});Q184=makeQuery(id+"F1.imprint","IMPRINT",FACE,{"disambiguationData":[TD([[makeQuery(id+"F1.imprint","IMPRINT",EDGE,{"disambiguationData":[TD([[subQ2,1.0]])],"derivedFrom":subQ1}),1.0]])]});}
            var Q185;
            {var subQ0=sQuery(id+"F1.wireOp",EDGE,"E9.3.0");var subQ1=sQuery(id+"F1.wireOp",EDGE,"E0");var subQ2=makeQuery(id+"F1.imprint","INTERSECT",VERTEX,{"derivedFrom":[subQ1,subQ0]});Q185=makeQuery(id+"F1.imprint","IMPRINT",FACE,{"disambiguationData":[TD([[makeQuery(id+"F1.imprint","IMPRINT",EDGE,{"disambiguationData":[TD([[subQ2,1.0]])],"derivedFrom":subQ1}),1.0]])]});}
            var Q186;
            {var subQ0=sQuery(id+"F1.wireOp",EDGE,"E9.3.1");var subQ1=sQuery(id+"F1.wireOp",EDGE,"E1.0");var subQ2=makeQuery(id+"F1.imprint","INTERSECT",VERTEX,{"derivedFrom":[subQ1,subQ0]});Q186=makeQuery(id+"F1.imprint","IMPRINT",FACE,{"disambiguationData":[TD([[makeQuery(id+"F1.imprint","IMPRINT",EDGE,{"disambiguationData":[TD([[subQ2,-1.0]])],"derivedFrom":subQ1}),1.0]])]});}
            var Q187;
            {var subQ0=sQuery(id+"F1.wireOp",EDGE,"E9.3.1");var subQ1=sQuery(id+"F1.wireOp",EDGE,"E3.0");var subQ2=makeQuery(id+"F1.imprint","INTERSECT",VERTEX,{"derivedFrom":[subQ1,subQ0]});Q187=makeQuery(id+"F1.imprint","IMPRINT",FACE,{"disambiguationData":[TD([[makeQuery(id+"F1.imprint","IMPRINT",EDGE,{"disambiguationData":[TD([[subQ2,-1.0]])],"derivedFrom":subQ1}),1.0]])]});}
            var Q188;
            {var subQ0=sQuery(id+"F1.wireOp",EDGE,"E9.2.0");var subQ1=sQuery(id+"F1.wireOp",EDGE,"E0");var subQ2=makeQuery(id+"F1.imprint","INTERSECT",VERTEX,{"derivedFrom":[subQ1,subQ0]});Q188=makeQuery(id+"F1.imprint","IMPRINT",FACE,{"disambiguationData":[TD([[makeQuery(id+"F1.imprint","IMPRINT",EDGE,{"disambiguationData":[TD([[subQ2,1.0]])],"derivedFrom":subQ1}),1.0]])]});}
            var Q189;
            {var subQ0=sQuery(id+"F1.wireOp",EDGE,"E9.1.0");var subQ1=sQuery(id+"F1.wireOp",EDGE,"E0");var subQ2=makeQuery(id+"F1.imprint","INTERSECT",VERTEX,{"derivedFrom":[subQ1,subQ0]});Q189=makeQuery(id+"F1.imprint","IMPRINT",FACE,{"disambiguationData":[TD([[makeQuery(id+"F1.imprint","IMPRINT",EDGE,{"disambiguationData":[TD([[subQ2,1.0]])],"derivedFrom":subQ1}),1.0]])]});}
            var Q190;
            {var subQ0=sQuery(id+"F1.wireOp",EDGE,"E9.1.0");var subQ1=sQuery(id+"F1.wireOp",EDGE,"E0");var subQ2=makeQuery(id+"F1.imprint","INTERSECT",VERTEX,{"derivedFrom":[subQ1,subQ0]});Q190=makeQuery(id+"F1.imprint","IMPRINT",FACE,{"disambiguationData":[TD([[makeQuery(id+"F1.imprint","IMPRINT",EDGE,{"disambiguationData":[TD([[subQ2,-1.0]])],"derivedFrom":subQ1}),1.0]])]});}
            var Q191;
            {var subQ0=sQuery(id+"F1.wireOp",EDGE,"E8");var subQ1=sQuery(id+"F1.wireOp",EDGE,"E0");var subQ2=makeQuery(id+"F1.imprint","INTERSECT",VERTEX,{"derivedFrom":[subQ1,subQ0]});Q191=makeQuery(id+"F1.imprint","IMPRINT",FACE,{"disambiguationData":[TD([[makeQuery(id+"F1.imprint","IMPRINT",EDGE,{"disambiguationData":[TD([[subQ2,-1.0]])],"derivedFrom":subQ1}),1.0]])]});}
            var Q192;
            {var subQ0=sQuery(id+"F1.wireOp",EDGE,"E6");var subQ1=sQuery(id+"F1.wireOp",EDGE,"E0");var subQ2=makeQuery(id+"F1.imprint","INTERSECT",VERTEX,{"derivedFrom":[subQ1,subQ0]});Q192=makeQuery(id+"F1.imprint","IMPRINT",FACE,{"disambiguationData":[TD([[makeQuery(id+"F1.imprint","IMPRINT",EDGE,{"disambiguationData":[TD([[subQ2,1.0]])],"derivedFrom":subQ1}),1.0]])]});}
            var Q193;
            {var subQ0=sQuery(id+"F1.wireOp",EDGE,"E9.14.0");var subQ1=sQuery(id+"F1.wireOp",EDGE,"E0");var subQ2=makeQuery(id+"F1.imprint","INTERSECT",VERTEX,{"derivedFrom":[subQ1,subQ0]});Q193=makeQuery(id+"F1.imprint","IMPRINT",FACE,{"disambiguationData":[TD([[makeQuery(id+"F1.imprint","IMPRINT",EDGE,{"disambiguationData":[TD([[subQ2,-1.0]])],"derivedFrom":subQ1}),1.0]])]});}
            var Q194;
            {var subQ0=sQuery(id+"F1.wireOp",EDGE,"E9.15.0");var subQ1=sQuery(id+"F1.wireOp",EDGE,"E0");var subQ2=makeQuery(id+"F1.imprint","INTERSECT",VERTEX,{"derivedFrom":[subQ1,subQ0]});Q194=makeQuery(id+"F1.imprint","IMPRINT",FACE,{"disambiguationData":[TD([[makeQuery(id+"F1.imprint","IMPRINT",EDGE,{"disambiguationData":[TD([[subQ2,1.0]])],"derivedFrom":subQ1}),1.0]])]});}
            var Q195;
            {var subQ0=sQuery(id+"F1.wireOp",EDGE,"E6");var subQ1=sQuery(id+"F1.wireOp",EDGE,"E0");var subQ2=makeQuery(id+"F1.imprint","INTERSECT",VERTEX,{"derivedFrom":[subQ1,subQ0]});Q195=makeQuery(id+"F1.imprint","IMPRINT",FACE,{"disambiguationData":[TD([[makeQuery(id+"F1.imprint","IMPRINT",EDGE,{"disambiguationData":[TD([[subQ2,-1.0]])],"derivedFrom":subQ1}),1.0]])]});}
            var Q196;
            {var subQ0=sQuery(id+"F1.wireOp",EDGE,"E9.2.0");var subQ1=sQuery(id+"F1.wireOp",EDGE,"E0");var subQ2=makeQuery(id+"F1.imprint","INTERSECT",VERTEX,{"derivedFrom":[subQ1,subQ0]});Q196=makeQuery(id+"F1.imprint","IMPRINT",FACE,{"disambiguationData":[TD([[makeQuery(id+"F1.imprint","IMPRINT",EDGE,{"disambiguationData":[TD([[subQ2,-1.0]])],"derivedFrom":subQ1}),1.0]])]});}
            var Q197;
            {var subQ0=sQuery(id+"F1.wireOp",EDGE,"E9.3.0");var subQ1=sQuery(id+"F1.wireOp",EDGE,"E0");var subQ2=makeQuery(id+"F1.imprint","INTERSECT",VERTEX,{"derivedFrom":[subQ1,subQ0]});Q197=makeQuery(id+"F1.imprint","IMPRINT",FACE,{"disambiguationData":[TD([[makeQuery(id+"F1.imprint","IMPRINT",EDGE,{"disambiguationData":[TD([[subQ2,-1.0]])],"derivedFrom":subQ1}),1.0]])]});}
            var Q198;
            {var subQ0=sQuery(id+"F1.wireOp",EDGE,"E9.4.0");var subQ1=sQuery(id+"F1.wireOp",EDGE,"E0");var subQ2=makeQuery(id+"F1.imprint","INTERSECT",VERTEX,{"derivedFrom":[subQ1,subQ0]});Q198=makeQuery(id+"F1.imprint","IMPRINT",FACE,{"disambiguationData":[TD([[makeQuery(id+"F1.imprint","IMPRINT",EDGE,{"disambiguationData":[TD([[subQ2,-1.0]])],"derivedFrom":subQ1}),1.0]])]});}
            var Q199;
            {var subQ0=sQuery(id+"F1.wireOp",EDGE,"E9.14.0");var subQ1=sQuery(id+"F1.wireOp",EDGE,"E2");var subQ2=makeQuery(id+"F1.imprint","INTERSECT",VERTEX,{"derivedFrom":[subQ1,subQ0]});Q199=makeQuery(id+"F1.imprint","IMPRINT",FACE,{"disambiguationData":[TD([[makeQuery(id+"F1.imprint","IMPRINT",EDGE,{"disambiguationData":[TD([[subQ2,-1.0]])],"derivedFrom":subQ1}),1.0]])]});}
            var Q200;
            {var subQ0=sQuery(id+"F1.wireOp",EDGE,"E9.13.0");var subQ1=sQuery(id+"F1.wireOp",EDGE,"E2");var subQ2=makeQuery(id+"F1.imprint","INTERSECT",VERTEX,{"derivedFrom":[subQ1,subQ0]});Q200=makeQuery(id+"F1.imprint","IMPRINT",FACE,{"disambiguationData":[TD([[makeQuery(id+"F1.imprint","IMPRINT",EDGE,{"disambiguationData":[TD([[subQ2,-1.0]])],"derivedFrom":subQ1}),1.0]])]});}
            var Q201;
            {var subQ0=sQuery(id+"F1.wireOp",EDGE,"E9.13.1");var subQ1=sQuery(id+"F1.wireOp",EDGE,"E2");var subQ2=makeQuery(id+"F1.imprint","INTERSECT",VERTEX,{"derivedFrom":[subQ1,subQ0]});Q201=makeQuery(id+"F1.imprint","IMPRINT",FACE,{"disambiguationData":[TD([[makeQuery(id+"F1.imprint","IMPRINT",EDGE,{"disambiguationData":[TD([[subQ2,1.0]])],"derivedFrom":subQ1}),1.0]])]});}
            var Q202;
            {var subQ0=sQuery(id+"F1.wireOp",EDGE,"E9.11.0");var subQ1=sQuery(id+"F1.wireOp",EDGE,"E2");var subQ2=makeQuery(id+"F1.imprint","INTERSECT",VERTEX,{"derivedFrom":[subQ1,subQ0]});Q202=makeQuery(id+"F1.imprint","IMPRINT",FACE,{"disambiguationData":[TD([[makeQuery(id+"F1.imprint","IMPRINT",EDGE,{"disambiguationData":[TD([[subQ2,-1.0]])],"derivedFrom":subQ1}),1.0]])]});}
            var Q203;
            {var subQ0=sQuery(id+"F1.wireOp",EDGE,"E9.9.0");var subQ1=sQuery(id+"F1.wireOp",EDGE,"E2");var subQ2=makeQuery(id+"F1.imprint","INTERSECT",VERTEX,{"derivedFrom":[subQ1,subQ0]});Q203=makeQuery(id+"F1.imprint","IMPRINT",FACE,{"disambiguationData":[TD([[makeQuery(id+"F1.imprint","IMPRINT",EDGE,{"disambiguationData":[TD([[subQ2,-1.0]])],"derivedFrom":subQ1}),1.0]])]});}
            var Q204;
            {var subQ0=sQuery(id+"F1.wireOp",EDGE,"E9.8.0");var subQ1=sQuery(id+"F1.wireOp",EDGE,"E2");var subQ2=makeQuery(id+"F1.imprint","INTERSECT",VERTEX,{"derivedFrom":[subQ1,subQ0]});Q204=makeQuery(id+"F1.imprint","IMPRINT",FACE,{"disambiguationData":[TD([[makeQuery(id+"F1.imprint","IMPRINT",EDGE,{"disambiguationData":[TD([[subQ2,-1.0]])],"derivedFrom":subQ1}),1.0]])]});}
            var Q205;
            {var subQ0=sQuery(id+"F1.wireOp",EDGE,"E9.7.0");var subQ1=sQuery(id+"F1.wireOp",EDGE,"E2");var subQ2=makeQuery(id+"F1.imprint","INTERSECT",VERTEX,{"derivedFrom":[subQ1,subQ0]});Q205=makeQuery(id+"F1.imprint","IMPRINT",FACE,{"disambiguationData":[TD([[makeQuery(id+"F1.imprint","IMPRINT",EDGE,{"disambiguationData":[TD([[subQ2,-1.0]])],"derivedFrom":subQ1}),1.0]])]});}
            var Q206;
            {var subQ0=sQuery(id+"F1.wireOp",EDGE,"E9.6.0");var subQ1=sQuery(id+"F1.wireOp",EDGE,"E2");var subQ2=makeQuery(id+"F1.imprint","INTERSECT",VERTEX,{"derivedFrom":[subQ1,subQ0]});Q206=makeQuery(id+"F1.imprint","IMPRINT",FACE,{"disambiguationData":[TD([[makeQuery(id+"F1.imprint","IMPRINT",EDGE,{"disambiguationData":[TD([[subQ2,-1.0]])],"derivedFrom":subQ1}),1.0]])]});}
            var Q207;
            {var subQ0=sQuery(id+"F1.wireOp",EDGE,"E9.4.1");var subQ1=sQuery(id+"F1.wireOp",EDGE,"E3.0");var subQ2=makeQuery(id+"F1.imprint","INTERSECT",VERTEX,{"derivedFrom":[subQ1,subQ0]});Q207=makeQuery(id+"F1.imprint","IMPRINT",FACE,{"disambiguationData":[TD([[makeQuery(id+"F1.imprint","IMPRINT",EDGE,{"disambiguationData":[TD([[subQ2,-1.0]])],"derivedFrom":subQ1}),1.0]])]});}
            var Q208;
            {var subQ0=sQuery(id+"F1.wireOp",EDGE,"E9.5.1");var subQ1=sQuery(id+"F1.wireOp",EDGE,"E3.0");var subQ2=makeQuery(id+"F1.imprint","INTERSECT",VERTEX,{"derivedFrom":[subQ1,subQ0]});Q208=makeQuery(id+"F1.imprint","IMPRINT",FACE,{"disambiguationData":[TD([[makeQuery(id+"F1.imprint","IMPRINT",EDGE,{"disambiguationData":[TD([[subQ2,-1.0]])],"derivedFrom":subQ1}),1.0]])]});}
            var Q209;
            {var subQ0=sQuery(id+"F1.wireOp",EDGE,"E9.10.0");var subQ1=sQuery(id+"F1.wireOp",EDGE,"E2");var subQ2=makeQuery(id+"F1.imprint","INTERSECT",VERTEX,{"derivedFrom":[subQ1,subQ0]});Q209=makeQuery(id+"F1.imprint","IMPRINT",FACE,{"disambiguationData":[TD([[makeQuery(id+"F1.imprint","IMPRINT",EDGE,{"disambiguationData":[TD([[subQ2,-1.0]])],"derivedFrom":subQ1}),1.0]])]});}
            extrude(context, id + "F2", {"entities" : qUnion([Q0, Q1, Q2, Q3, Q4, Q5, Q6, Q7, Q8, Q9, Q10, Q11, Q12, Q13, Q14, Q15, Q16, Q17, Q18, Q19, Q20, Q21, Q22, Q23, Q24, Q25, Q26, Q27, Q28, Q29, Q30, Q31, Q32, Q33, Q34, Q35, Q36, Q37, Q38, Q39, Q40, Q41, Q42, Q43, Q44, Q45, Q46, Q47, Q48, Q49, Q50, Q51, Q52, Q53, Q54, Q55, Q56, Q57, Q58, Q59, Q60, Q61, Q62, Q63, Q64, Q65, Q66, Q67, Q68, Q69, Q70, Q71, Q72, Q73, Q74, Q75, Q76, Q77, Q78, Q79, Q80, Q81, Q82, Q83, Q84, Q85, Q86, Q87, Q88, Q89, Q90, Q91, Q92, Q93, Q94, Q95, Q96, Q97, Q98, Q99, Q100, Q101, Q102, Q103, Q104, Q105, Q106, Q107, Q108, Q109, Q110, Q111, Q112, Q113, Q114, Q115, Q116, Q117, Q118, Q119, Q120, Q121, Q122, Q123, Q124, Q125, Q126, Q127, Q128, Q129, Q130, Q131, Q132, Q133, Q134, Q135, Q136, Q137, Q138, Q139, Q140, Q141, Q142, Q143, Q144, Q145, Q146, Q147, Q148, Q149, Q150, Q151, Q152, Q153, Q154, Q155, Q156, Q157, Q158, Q159, Q160, Q161, Q162, Q163, Q164, Q165, Q166, Q167, Q168, Q169, Q170, Q171, Q172, Q173, Q174, Q175, Q176, Q177, Q178, Q179, Q180, Q181, Q182, Q183, Q184, Q185, Q186, Q187, Q188, Q189, Q190, Q191, Q192, Q193, Q194, Q195, Q196, Q197, Q198, Q199, Q200, Q201, Q202, Q203, Q204, Q205, Q206, Q207, Q208, Q209]), "oppositeDirection" : true, "depth" : (getVariable(context, 'b')) * mm, "offsetDistance" : 25 * mm});
        }
    });
